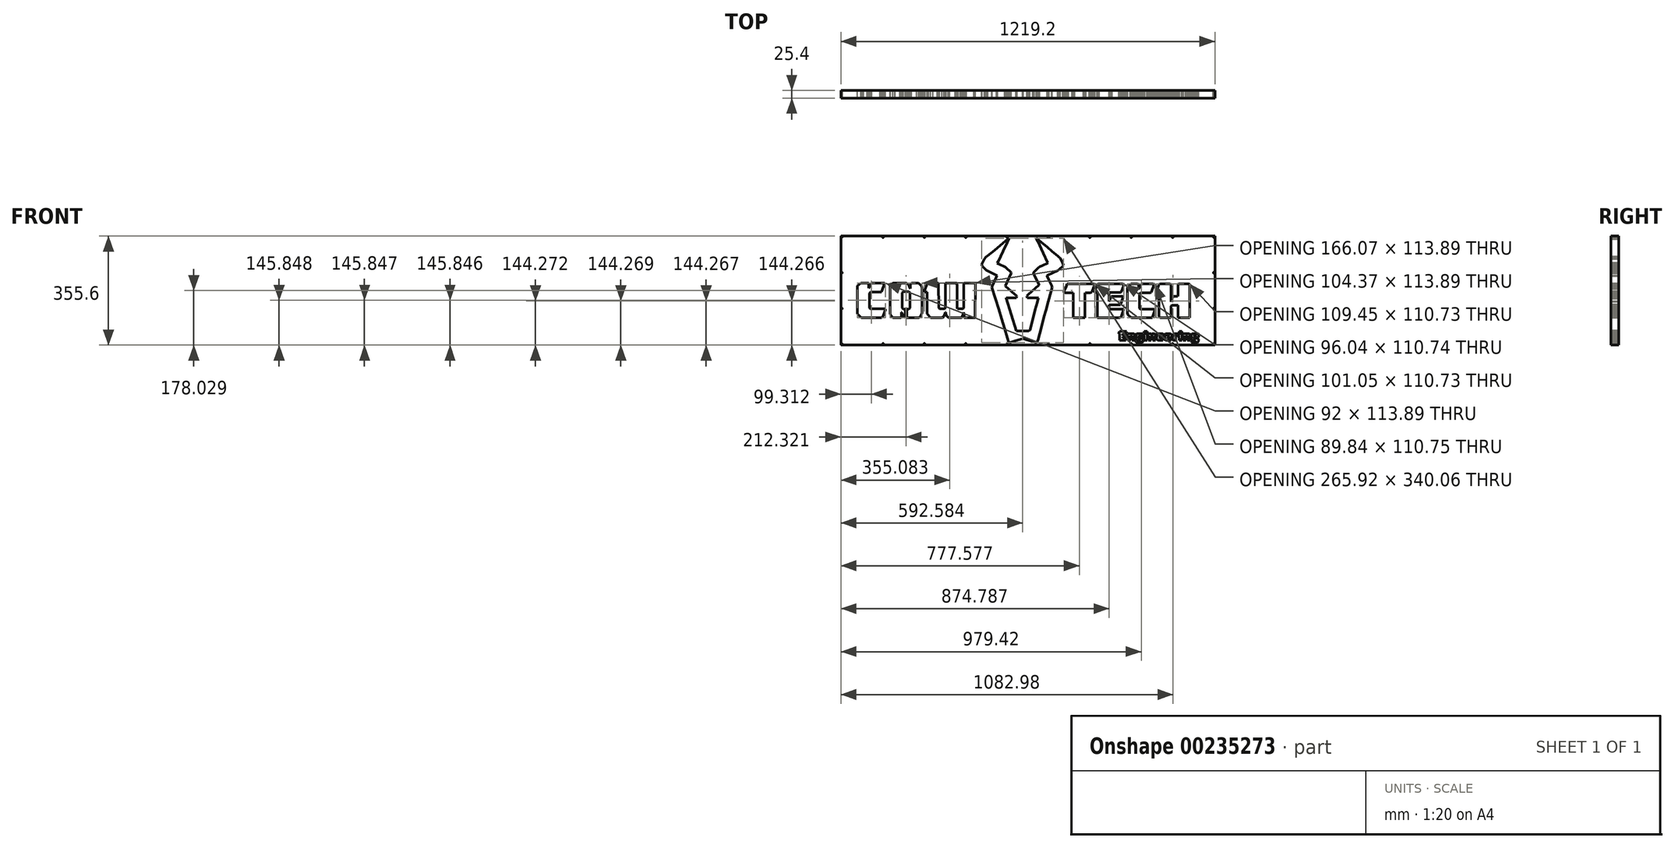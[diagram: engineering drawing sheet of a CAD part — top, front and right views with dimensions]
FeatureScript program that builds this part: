
annotation { "Feature Type Name" : "Feature", "Feature Type Description" : "" }
export const myFeature = defineFeature(function(context is Context, id is Id, definition is map)
    precondition{}
    {
        {
            var Q0;
            Q0=qCreatedBy(makeId("Front.planeOp"),FACE);
            var sketch = newSketch(context, id + "F0", { "sketchPlane" : qUnion([Q0])});
            skLineSegment(sketch, "E0.bottom", {"start": v(609.6, -177.8) * mm, "end": v(-609.6, -177.8) * mm});
            skLineSegment(sketch, "E0.top", {"start": v(609.6, 177.8) * mm, "end": v(-609.6, 177.8) * mm});
            skLineSegment(sketch, "E0.left", {"start": v(609.6, -177.8) * mm, "end": v(609.6, 177.8) * mm});
            skLineSegment(sketch, "E0.right", {"start": v(-609.6, -177.8) * mm, "end": v(-609.6, 177.8) * mm});
            skPoint(sketch, "E0.middle", {"position": v(0, 0) * mm});
            skLineSegment(sketch, "E1.top", {"start": v(-606.8, -175) * mm, "end": v(606.8, -175) * mm});
            skLineSegment(sketch, "E1.left", {"start": v(-606.8, 175) * mm, "end": v(-606.8, -175) * mm});
            skLineSegment(sketch, "E1.right", {"start": v(606.8, 175) * mm, "end": v(606.8, -175) * mm});
            skCircle(sketch, "E2", {"center": v(-606.8, 175) * mm, "radius": 2.29 * mm});
            skCircle(sketch, "E3.1.0.0", {"center": v(-471.96, 175) * mm, "radius": 2.29 * mm});
            skCircle(sketch, "E3.2.0.0", {"center": v(-337.11, 175) * mm, "radius": 2.29 * mm});
            skCircle(sketch, "E3.3.0.0", {"center": v(-202.27, 175) * mm, "radius": 2.29 * mm});
            skCircle(sketch, "E3.4.0.0", {"center": v(-67.42, 175) * mm, "radius": 2.29 * mm});
            skCircle(sketch, "E3.5.0.0", {"center": v(67.42, 175) * mm, "radius": 2.29 * mm});
            skCircle(sketch, "E3.6.0.0", {"center": v(202.27, 175) * mm, "radius": 2.29 * mm});
            skCircle(sketch, "E3.7.0.0", {"center": v(337.11, 175) * mm, "radius": 2.29 * mm});
            skCircle(sketch, "E3.8.0.0", {"center": v(471.96, 175) * mm, "radius": 2.29 * mm});
            skCircle(sketch, "E3.9.0.0", {"center": v(606.8, 175) * mm, "radius": 2.29 * mm});
            skLineSegment(sketch, "E3.direction1", {"start": v(-606.8, 175) * mm, "end": v(-471.96, 175) * mm, "construction": true});
            skLineSegment(sketch, "E4", {"start": v(0, 0) * mm, "end": v(-450.1, 0) * mm, "construction": true});
            skCircle(sketch, "E5.MirrorC", {"center": v(-471.96, -175) * mm, "radius": 2.29 * mm});
            skCircle(sketch, "E6.MirrorC", {"center": v(-606.8, -175) * mm, "radius": 2.29 * mm});
            skCircle(sketch, "E7.MirrorC", {"center": v(-337.11, -175) * mm, "radius": 2.29 * mm});
            skCircle(sketch, "E8.MirrorC", {"center": v(-202.27, -175) * mm, "radius": 2.29 * mm});
            skCircle(sketch, "E9.MirrorC", {"center": v(-67.42, -175) * mm, "radius": 2.29 * mm});
            skCircle(sketch, "E10.MirrorC", {"center": v(67.42, -175) * mm, "radius": 2.29 * mm});
            skCircle(sketch, "E11.MirrorC", {"center": v(202.27, -175) * mm, "radius": 2.29 * mm});
            skCircle(sketch, "E12.MirrorC", {"center": v(337.11, -175) * mm, "radius": 2.29 * mm});
            skCircle(sketch, "E13.MirrorC", {"center": v(471.96, -175) * mm, "radius": 2.29 * mm});
            skCircle(sketch, "E14.MirrorC", {"center": v(606.8, -175) * mm, "radius": 2.29 * mm});
            skCircle(sketch, "E15.1.0.0", {"center": v(-606.8, 58.34) * mm, "radius": 2.29 * mm});
            skCircle(sketch, "E15.2.0.0", {"center": v(-606.8, -58.34) * mm, "radius": 2.29 * mm});
            skLineSegment(sketch, "E15.direction1", {"start": v(-606.8, 175) * mm, "end": v(-606.8, 58.34) * mm, "construction": true});
            skLineSegment(sketch, "E16", {"start": v(0, 0) * mm, "end": v(0, 134.11) * mm, "construction": true});
            skCircle(sketch, "E17.MirrorC", {"center": v(606.8, 58.34) * mm, "radius": 2.29 * mm});
            skCircle(sketch, "E18.MirrorC", {"center": v(606.8, -58.34) * mm, "radius": 2.29 * mm});
            skSolve(sketch);
        }
        {
            var Q0;
            Q0=makeQuery(id+"F0.imprint","IMPRINT",FACE,{"disambiguationData":[TD([[makeQuery(id+"F0.imprint","IMPRINT",EDGE,{"derivedFrom":sQuery(id+"F0.wireOp",EDGE,"E0.bottom")}),-1.0]])]});
            var sketch = newSketch(context, id + "F1", { "sketchPlane" : qUnion([Q0])});
            skLineSegment(sketch, "E19", {"start": v(30.23, -169.78) * mm, "end": v(23.8, -168.03) * mm});
            skLineSegment(sketch, "E20", {"start": v(23.8, -168.03) * mm, "end": v(-7.37, -159.28) * mm});
            skLineSegment(sketch, "E21", {"start": v(-7.37, -159.28) * mm, "end": v(-14.2, -157.3) * mm});
            skLineSegment(sketch, "E22", {"start": v(-14.2, -157.3) * mm, "end": v(-16.57, -157.28) * mm});
            skLineSegment(sketch, "E23", {"start": v(-16.57, -157.28) * mm, "end": v(-40.15, -164.01) * mm});
            skLineSegment(sketch, "E24", {"start": v(-40.15, -164.01) * mm, "end": v(-59.48, -169.5) * mm});
            skLineSegment(sketch, "E25", {"start": v(-59.48, -169.5) * mm, "end": v(-60.97, -169.8) * mm});
            skLineSegment(sketch, "E26", {"start": v(-60.97, -169.8) * mm, "end": v(-62.42, -166.98) * mm});
            skLineSegment(sketch, "E27", {"start": v(-62.42, -166.98) * mm, "end": v(-66.22, -154.79) * mm});
            skLineSegment(sketch, "E28", {"start": v(-66.22, -154.79) * mm, "end": v(-75.53, -124.27) * mm});
            skLineSegment(sketch, "E29", {"start": v(-75.53, -124.27) * mm, "end": v(-85.6, -91.16) * mm});
            skLineSegment(sketch, "E30", {"start": v(-85.6, -91.16) * mm, "end": v(-95.08, -60.42) * mm});
            skLineSegment(sketch, "E31", {"start": v(-95.08, -60.42) * mm, "end": v(-105.76, -25.19) * mm});
            skLineSegment(sketch, "E32", {"start": v(-105.76, -25.19) * mm, "end": v(-116.9, 10.67) * mm});
            skLineSegment(sketch, "E33", {"start": v(-116.9, 10.67) * mm, "end": v(-116.63, 13.72) * mm});
            skLineSegment(sketch, "E34", {"start": v(-116.63, 13.72) * mm, "end": v(-103.29, 42.19) * mm});
            skLineSegment(sketch, "E35", {"start": v(-103.29, 42.19) * mm, "end": v(-100.59, 47.97) * mm});
            skLineSegment(sketch, "E36", {"start": v(-100.59, 47.97) * mm, "end": v(-100.17, 49.2) * mm});
            skLineSegment(sketch, "E37", {"start": v(-100.17, 49.2) * mm, "end": v(-101.67, 50.11) * mm});
            skLineSegment(sketch, "E38", {"start": v(-101.67, 50.11) * mm, "end": v(-120.54, 59.03) * mm});
            skLineSegment(sketch, "E39", {"start": v(-120.54, 59.03) * mm, "end": v(-130.76, 63.84) * mm});
            skLineSegment(sketch, "E40", {"start": v(-130.76, 63.84) * mm, "end": v(-135.19, 66.9) * mm});
            skLineSegment(sketch, "E41", {"start": v(-135.19, 66.9) * mm, "end": v(-148.63, 80.22) * mm});
            skLineSegment(sketch, "E42", {"start": v(-148.63, 80.22) * mm, "end": v(-149.7, 81.57) * mm});
            skLineSegment(sketch, "E43", {"start": v(-149.7, 81.57) * mm, "end": v(-149.98, 85.04) * mm});
            skLineSegment(sketch, "E44", {"start": v(-149.98, 85.04) * mm, "end": v(-147.5, 90.38) * mm});
            skLineSegment(sketch, "E45", {"start": v(-147.5, 90.38) * mm, "end": v(-141.5, 103.31) * mm});
            skLineSegment(sketch, "E46", {"start": v(-141.5, 103.31) * mm, "end": v(-137.04, 109.06) * mm});
            skLineSegment(sketch, "E47", {"start": v(-137.04, 109.06) * mm, "end": v(-115.55, 126.68) * mm});
            skLineSegment(sketch, "E48", {"start": v(-115.55, 126.68) * mm, "end": v(-100.34, 139.14) * mm});
            skLineSegment(sketch, "E49", {"start": v(-100.34, 139.14) * mm, "end": v(-71.43, 162.81) * mm});
            skLineSegment(sketch, "E50", {"start": v(-71.43, 162.81) * mm, "end": v(-63.4, 169.3) * mm});
            skLineSegment(sketch, "E51", {"start": v(-63.4, 169.3) * mm, "end": v(-61.47, 170.18) * mm});
            skLineSegment(sketch, "E52", {"start": v(-61.47, 170.18) * mm, "end": v(-61.97, 168.1) * mm});
            skLineSegment(sketch, "E53", {"start": v(-61.97, 168.1) * mm, "end": v(-66.6, 158.34) * mm});
            skLineSegment(sketch, "E54", {"start": v(-66.6, 158.34) * mm, "end": v(-80.63, 128.83) * mm});
            skLineSegment(sketch, "E55", {"start": v(-80.63, 128.83) * mm, "end": v(-96.44, 95.54) * mm});
            skLineSegment(sketch, "E56", {"start": v(-96.44, 95.54) * mm, "end": v(-99.34, 89.4) * mm});
            skLineSegment(sketch, "E57", {"start": v(-99.34, 89.4) * mm, "end": v(-97.9, 88.08) * mm});
            skLineSegment(sketch, "E58", {"start": v(-97.9, 88.08) * mm, "end": v(-91.68, 85.14) * mm});
            skLineSegment(sketch, "E59", {"start": v(-91.68, 85.14) * mm, "end": v(-75.87, 77.81) * mm});
            skLineSegment(sketch, "E60", {"start": v(-75.87, 77.81) * mm, "end": v(-73.22, 76.53) * mm});
            skLineSegment(sketch, "E61", {"start": v(-73.22, 76.53) * mm, "end": v(-70.04, 74.26) * mm});
            skLineSegment(sketch, "E62", {"start": v(-70.04, 74.26) * mm, "end": v(-55.8, 59.98) * mm});
            skLineSegment(sketch, "E63", {"start": v(-55.8, 59.98) * mm, "end": v(-53.65, 57.54) * mm});
            skLineSegment(sketch, "E64", {"start": v(-53.65, 57.54) * mm, "end": v(-73.23, 15.55) * mm});
            skLineSegment(sketch, "E65", {"start": v(-73.23, 15.55) * mm, "end": v(-71.4, 13.34) * mm});
            skLineSegment(sketch, "E66", {"start": v(-71.4, 13.34) * mm, "end": v(-63.63, 6.53) * mm});
            skLineSegment(sketch, "E67", {"start": v(-63.63, 6.53) * mm, "end": v(-42.1, -12.55) * mm});
            skLineSegment(sketch, "E68", {"start": v(-42.1, -12.55) * mm, "end": v(-37.9, -16.32) * mm});
            skLineSegment(sketch, "E69", {"start": v(-37.9, -16.32) * mm, "end": v(-36.86, -18.7) * mm});
            skLineSegment(sketch, "E70", {"start": v(-36.86, -18.7) * mm, "end": v(-37.04, -23.65) * mm});
            skLineSegment(sketch, "E71", {"start": v(-37.04, -23.65) * mm, "end": v(-39.3, -24.2) * mm});
            skLineSegment(sketch, "E72", {"start": v(-39.3, -24.2) * mm, "end": v(-63.15, -24.17) * mm});
            skLineSegment(sketch, "E73", {"start": v(-63.15, -24.17) * mm, "end": v(-68.56, -24.16) * mm});
            skLineSegment(sketch, "E74", {"start": v(-68.56, -24.16) * mm, "end": v(-70.2, -24.4) * mm});
            skLineSegment(sketch, "E75", {"start": v(-70.2, -24.4) * mm, "end": v(-70.3, -25.24) * mm});
            skLineSegment(sketch, "E76", {"start": v(-70.3, -25.24) * mm, "end": v(-37.92, -131.17) * mm});
            skLineSegment(sketch, "E77", {"start": v(-37.92, -131.17) * mm, "end": v(-35.1, -131.64) * mm});
            skLineSegment(sketch, "E78", {"start": v(-35.1, -131.64) * mm, "end": v(-22.05, -131.65) * mm});
            skLineSegment(sketch, "E79", {"start": v(-22.05, -131.65) * mm, "end": v(2.79, -131.65) * mm});
            skLineSegment(sketch, "E80", {"start": v(2.79, -131.65) * mm, "end": v(6.44, -128.86) * mm});
            skLineSegment(sketch, "E81", {"start": v(6.44, -128.86) * mm, "end": v(16.74, -90.46) * mm});
            skLineSegment(sketch, "E82", {"start": v(16.74, -90.46) * mm, "end": v(23.97, -63.43) * mm});
            skLineSegment(sketch, "E83", {"start": v(23.97, -63.43) * mm, "end": v(30.71, -38.05) * mm});
            skLineSegment(sketch, "E84", {"start": v(30.71, -38.05) * mm, "end": v(34.05, -25.73) * mm});
            skLineSegment(sketch, "E85", {"start": v(34.05, -25.73) * mm, "end": v(34.47, -23.95) * mm});
            skLineSegment(sketch, "E86", {"start": v(34.47, -23.95) * mm, "end": v(25.31, -24.01) * mm});
            skLineSegment(sketch, "E87", {"start": v(25.31, -24.01) * mm, "end": v(16.22, -24.14) * mm});
            skLineSegment(sketch, "E88", {"start": v(16.22, -24.14) * mm, "end": v(7.12, -24.15) * mm});
            skLineSegment(sketch, "E89", {"start": v(7.12, -24.15) * mm, "end": v(-1.94, -24.11) * mm});
            skLineSegment(sketch, "E90", {"start": v(-1.94, -24.11) * mm, "end": v(-2.7, -17.5) * mm});
            skLineSegment(sketch, "E91", {"start": v(-2.7, -17.5) * mm, "end": v(-2.02, -16.25) * mm});
            skLineSegment(sketch, "E92", {"start": v(-2.02, -16.25) * mm, "end": v(0.16, -14.27) * mm});
            skLineSegment(sketch, "E93", {"start": v(0.16, -14.27) * mm, "end": v(25.23, 7.85) * mm});
            skLineSegment(sketch, "E94", {"start": v(25.23, 7.85) * mm, "end": v(34.84, 16.29) * mm});
            skLineSegment(sketch, "E95", {"start": v(34.84, 16.29) * mm, "end": v(36.37, 17.75) * mm});
            skLineSegment(sketch, "E96", {"start": v(36.37, 17.75) * mm, "end": v(35.74, 19.52) * mm});
            skLineSegment(sketch, "E97", {"start": v(35.74, 19.52) * mm, "end": v(21.07, 50.9) * mm});
            skLineSegment(sketch, "E98", {"start": v(21.07, 50.9) * mm, "end": v(18.53, 56.5) * mm});
            skLineSegment(sketch, "E99", {"start": v(18.53, 56.5) * mm, "end": v(18.85, 58.73) * mm});
            skLineSegment(sketch, "E100", {"start": v(18.85, 58.73) * mm, "end": v(20.87, 60.88) * mm});
            skLineSegment(sketch, "E101", {"start": v(20.87, 60.88) * mm, "end": v(34.76, 74.81) * mm});
            skLineSegment(sketch, "E102", {"start": v(34.76, 74.81) * mm, "end": v(38.96, 77.77) * mm});
            skLineSegment(sketch, "E103", {"start": v(38.96, 77.77) * mm, "end": v(48.1, 81.96) * mm});
            skLineSegment(sketch, "E104", {"start": v(48.1, 81.96) * mm, "end": v(63.89, 89.36) * mm});
            skLineSegment(sketch, "E105", {"start": v(63.89, 89.36) * mm, "end": v(65.07, 90.07) * mm});
            skLineSegment(sketch, "E106", {"start": v(65.07, 90.07) * mm, "end": v(64.62, 91.66) * mm});
            skLineSegment(sketch, "E107", {"start": v(64.62, 91.66) * mm, "end": v(50.38, 121.88) * mm});
            skLineSegment(sketch, "E108", {"start": v(50.38, 121.88) * mm, "end": v(31.98, 161) * mm});
            skLineSegment(sketch, "E109", {"start": v(31.98, 161) * mm, "end": v(28.5, 168.33) * mm});
            skLineSegment(sketch, "E110", {"start": v(28.5, 168.33) * mm, "end": v(27.95, 170.26) * mm});
            skLineSegment(sketch, "E111", {"start": v(27.95, 170.26) * mm, "end": v(29.5, 169.48) * mm});
            skLineSegment(sketch, "E112", {"start": v(29.5, 169.48) * mm, "end": v(43.55, 157.93) * mm});
            skLineSegment(sketch, "E113", {"start": v(43.55, 157.93) * mm, "end": v(64.17, 140.8) * mm});
            skLineSegment(sketch, "E114", {"start": v(64.17, 140.8) * mm, "end": v(78.56, 128.9) * mm});
            skLineSegment(sketch, "E115", {"start": v(78.56, 128.9) * mm, "end": v(98.53, 112.54) * mm});
            skLineSegment(sketch, "E116", {"start": v(98.53, 112.54) * mm, "end": v(102.86, 108.9) * mm});
            skLineSegment(sketch, "E117", {"start": v(102.86, 108.9) * mm, "end": v(105.66, 105.22) * mm});
            skLineSegment(sketch, "E118", {"start": v(105.66, 105.22) * mm, "end": v(113.07, 89.43) * mm});
            skLineSegment(sketch, "E119", {"start": v(113.07, 89.43) * mm, "end": v(115.95, 83.17) * mm});
            skLineSegment(sketch, "E120", {"start": v(115.95, 83.17) * mm, "end": v(113.23, 79.66) * mm});
            skLineSegment(sketch, "E121", {"start": v(113.23, 79.66) * mm, "end": v(103.17, 69.55) * mm});
            skLineSegment(sketch, "E122", {"start": v(103.17, 69.55) * mm, "end": v(97.19, 65.33) * mm});
            skLineSegment(sketch, "E123", {"start": v(97.19, 65.33) * mm, "end": v(64.08, 49.76) * mm});
            skLineSegment(sketch, "E124", {"start": v(64.08, 49.76) * mm, "end": v(62.67, 49.02) * mm});
            skLineSegment(sketch, "E125", {"start": v(62.67, 49.02) * mm, "end": v(63.09, 46.83) * mm});
            skLineSegment(sketch, "E126", {"start": v(63.09, 46.83) * mm, "end": v(71.73, 28.37) * mm});
            skLineSegment(sketch, "E127", {"start": v(71.73, 28.37) * mm, "end": v(77.47, 16.14) * mm});
            skLineSegment(sketch, "E128", {"start": v(77.47, 16.14) * mm, "end": v(78.48, 13.9) * mm});
            skLineSegment(sketch, "E129", {"start": v(78.48, 13.9) * mm, "end": v(78.73, 10.1) * mm});
            skLineSegment(sketch, "E130", {"start": v(78.73, 10.1) * mm, "end": v(74.92, -3.87) * mm});
            skLineSegment(sketch, "E131", {"start": v(74.92, -3.87) * mm, "end": v(66.64, -34.94) * mm});
            skLineSegment(sketch, "E132", {"start": v(66.64, -34.94) * mm, "end": v(58.69, -64.32) * mm});
            skLineSegment(sketch, "E133", {"start": v(58.69, -64.32) * mm, "end": v(53.13, -85.2) * mm});
            skLineSegment(sketch, "E134", {"start": v(53.13, -85.2) * mm, "end": v(43.46, -121.22) * mm});
            skLineSegment(sketch, "E135", {"start": v(43.46, -121.22) * mm, "end": v(33.08, -159.87) * mm});
            skLineSegment(sketch, "E136", {"start": v(33.08, -159.87) * mm, "end": v(31.36, -166.52) * mm});
            skLineSegment(sketch, "E137", {"start": v(31.36, -166.52) * mm, "end": v(30.23, -169.78) * mm});
            skLineSegment(sketch, "E138", {"start": v(-208.3, 24.16) * mm, "end": v(-204.68, 24.98) * mm});
            skLineSegment(sketch, "E139", {"start": v(-204.68, 24.98) * mm, "end": v(-175.42, 24.98) * mm});
            skLineSegment(sketch, "E140", {"start": v(-175.42, 24.98) * mm, "end": v(-171.73, 24.14) * mm});
            skLineSegment(sketch, "E141", {"start": v(-171.73, 24.14) * mm, "end": v(-171.48, 22.8) * mm});
            skLineSegment(sketch, "E142", {"start": v(-171.48, 22.8) * mm, "end": v(-171.52, -87.12) * mm});
            skLineSegment(sketch, "E143", {"start": v(-171.52, -87.12) * mm, "end": v(-171.9, -88.4) * mm});
            skLineSegment(sketch, "E144", {"start": v(-171.9, -88.4) * mm, "end": v(-174.72, -88.86) * mm});
            skLineSegment(sketch, "E145", {"start": v(-174.72, -88.86) * mm, "end": v(-204.36, -88.87) * mm});
            skLineSegment(sketch, "E146", {"start": v(-204.36, -88.87) * mm, "end": v(-207.65, -87.94) * mm});
            skLineSegment(sketch, "E147", {"start": v(-207.65, -87.94) * mm, "end": v(-207.98, -79.5) * mm});
            skLineSegment(sketch, "E148", {"start": v(-207.98, -79.5) * mm, "end": v(-208.5, -70.9) * mm});
            skLineSegment(sketch, "E149", {"start": v(-208.5, -70.9) * mm, "end": v(-209.25, -72.45) * mm});
            skLineSegment(sketch, "E150", {"start": v(-209.25, -72.45) * mm, "end": v(-214.5, -84.87) * mm});
            skLineSegment(sketch, "E151", {"start": v(-214.5, -84.87) * mm, "end": v(-215.58, -87.26) * mm});
            skLineSegment(sketch, "E152", {"start": v(-215.58, -87.26) * mm, "end": v(-217.59, -88.72) * mm});
            skLineSegment(sketch, "E153", {"start": v(-217.59, -88.72) * mm, "end": v(-220.58, -88.9) * mm});
            skLineSegment(sketch, "E154", {"start": v(-220.58, -88.9) * mm, "end": v(-254.34, -88.88) * mm});
            skLineSegment(sketch, "E155", {"start": v(-254.34, -88.88) * mm, "end": v(-258.82, -88.5) * mm});
            skLineSegment(sketch, "E156", {"start": v(-258.82, -88.5) * mm, "end": v(-266.47, -81.36) * mm});
            skLineSegment(sketch, "E157", {"start": v(-266.47, -81.36) * mm, "end": v(-267.26, -74.3) * mm});
            skLineSegment(sketch, "E158", {"start": v(-267.26, -74.3) * mm, "end": v(-267.28, -70.23) * mm});
            skLineSegment(sketch, "E159", {"start": v(-267.28, -70.23) * mm, "end": v(-268.39, -71.11) * mm});
            skLineSegment(sketch, "E160", {"start": v(-268.39, -71.11) * mm, "end": v(-274.05, -84.59) * mm});
            skLineSegment(sketch, "E161", {"start": v(-274.05, -84.59) * mm, "end": v(-280.66, -88.9) * mm});
            skLineSegment(sketch, "E162", {"start": v(-280.66, -88.9) * mm, "end": v(-291.53, -88.9) * mm});
            skLineSegment(sketch, "E163", {"start": v(-291.53, -88.9) * mm, "end": v(-309.54, -88.88) * mm});
            skLineSegment(sketch, "E164", {"start": v(-309.54, -88.88) * mm, "end": v(-317.01, -88.4) * mm});
            skLineSegment(sketch, "E165", {"start": v(-317.01, -88.4) * mm, "end": v(-328.06, -75.8) * mm});
            skLineSegment(sketch, "E166", {"start": v(-328.06, -75.8) * mm, "end": v(-328.23, -68.3) * mm});
            skLineSegment(sketch, "E167", {"start": v(-328.23, -68.3) * mm, "end": v(-328.25, -9.4) * mm});
            skLineSegment(sketch, "E168", {"start": v(-328.25, -9.4) * mm, "end": v(-328.75, -4.8) * mm});
            skLineSegment(sketch, "E169", {"start": v(-328.75, -4.8) * mm, "end": v(-337.55, -4.2) * mm});
            skLineSegment(sketch, "E170", {"start": v(-337.55, -4.2) * mm, "end": v(-337.47, -1.32) * mm});
            skLineSegment(sketch, "E171", {"start": v(-337.47, -1.32) * mm, "end": v(-330.82, 15.79) * mm});
            skLineSegment(sketch, "E172", {"start": v(-330.82, 15.79) * mm, "end": v(-328.78, 21.02) * mm});
            skLineSegment(sketch, "E173", {"start": v(-328.78, 21.02) * mm, "end": v(-327.17, 24.6) * mm});
            skLineSegment(sketch, "E174", {"start": v(-327.17, 24.6) * mm, "end": v(-323.07, 24.97) * mm});
            skLineSegment(sketch, "E175", {"start": v(-323.07, 24.97) * mm, "end": v(-295.31, 24.98) * mm});
            skLineSegment(sketch, "E176", {"start": v(-295.31, 24.98) * mm, "end": v(-291.27, 24.25) * mm});
            skLineSegment(sketch, "E177", {"start": v(-291.27, 24.25) * mm, "end": v(-290.88, 19.48) * mm});
            skLineSegment(sketch, "E178", {"start": v(-290.88, 19.48) * mm, "end": v(-290.87, -52.93) * mm});
            skLineSegment(sketch, "E179", {"start": v(-290.87, -52.93) * mm, "end": v(-290.82, -56.3) * mm});
            skLineSegment(sketch, "E180", {"start": v(-290.82, -56.3) * mm, "end": v(-287.45, -59.5) * mm});
            skLineSegment(sketch, "E181", {"start": v(-287.45, -59.5) * mm, "end": v(-271.7, -59.5) * mm});
            skLineSegment(sketch, "E182", {"start": v(-271.7, -59.5) * mm, "end": v(-268.8, -56.5) * mm});
            skLineSegment(sketch, "E183", {"start": v(-268.8, -56.5) * mm, "end": v(-268.78, -53.13) * mm});
            skLineSegment(sketch, "E184", {"start": v(-268.78, -53.13) * mm, "end": v(-268.77, 19.27) * mm});
            skLineSegment(sketch, "E185", {"start": v(-268.77, 19.27) * mm, "end": v(-268.61, 24.22) * mm});
            skLineSegment(sketch, "E186", {"start": v(-268.61, 24.22) * mm, "end": v(-265.96, 24.9) * mm});
            skLineSegment(sketch, "E187", {"start": v(-265.96, 24.9) * mm, "end": v(-260.34, 25) * mm});
            skLineSegment(sketch, "E188", {"start": v(-260.34, 25) * mm, "end": v(-236.33, 24.98) * mm});
            skLineSegment(sketch, "E189", {"start": v(-236.33, 24.98) * mm, "end": v(-231.75, 24.7) * mm});
            skLineSegment(sketch, "E190", {"start": v(-231.75, 24.7) * mm, "end": v(-231.11, 22.07) * mm});
            skLineSegment(sketch, "E191", {"start": v(-231.11, 22.07) * mm, "end": v(-231.06, 18.32) * mm});
            skLineSegment(sketch, "E192", {"start": v(-231.06, 18.32) * mm, "end": v(-231.05, -52.96) * mm});
            skLineSegment(sketch, "E193", {"start": v(-231.05, -52.96) * mm, "end": v(-230.93, -57.08) * mm});
            skLineSegment(sketch, "E194", {"start": v(-230.93, -57.08) * mm, "end": v(-228.8, -59.35) * mm});
            skLineSegment(sketch, "E195", {"start": v(-228.8, -59.35) * mm, "end": v(-226.57, -59.53) * mm});
            skLineSegment(sketch, "E196", {"start": v(-226.57, -59.53) * mm, "end": v(-212.7, -59.53) * mm});
            skLineSegment(sketch, "E197", {"start": v(-212.7, -59.53) * mm, "end": v(-211.2, -59.46) * mm});
            skLineSegment(sketch, "E198", {"start": v(-211.2, -59.46) * mm, "end": v(-208.8, -57.13) * mm});
            skLineSegment(sketch, "E199", {"start": v(-208.8, -57.13) * mm, "end": v(-208.74, -53.38) * mm});
            skLineSegment(sketch, "E200", {"start": v(-208.74, -53.38) * mm, "end": v(-208.73, 19.4) * mm});
            skLineSegment(sketch, "E201", {"start": v(-208.73, 19.4) * mm, "end": v(-208.3, 24.16) * mm});
            skLineSegment(sketch, "E202", {"start": v(-411.92, -70.4) * mm, "end": v(-411.93, -83.89) * mm});
            skLineSegment(sketch, "E203", {"start": v(-411.93, -83.89) * mm, "end": v(-412.13, -87.25) * mm});
            skLineSegment(sketch, "E204", {"start": v(-412.13, -87.25) * mm, "end": v(-413.62, -88.69) * mm});
            skLineSegment(sketch, "E205", {"start": v(-413.62, -88.69) * mm, "end": v(-416.6, -88.89) * mm});
            skLineSegment(sketch, "E206", {"start": v(-416.6, -88.89) * mm, "end": v(-433.86, -88.87) * mm});
            skLineSegment(sketch, "E207", {"start": v(-433.86, -88.87) * mm, "end": v(-440.16, -88.15) * mm});
            skLineSegment(sketch, "E208", {"start": v(-440.16, -88.15) * mm, "end": v(-448.86, -77.51) * mm});
            skLineSegment(sketch, "E209", {"start": v(-448.86, -77.51) * mm, "end": v(-449.46, -69.3) * mm});
            skLineSegment(sketch, "E210", {"start": v(-449.46, -69.3) * mm, "end": v(-449.46, 6.06) * mm});
            skLineSegment(sketch, "E211", {"start": v(-449.46, 6.06) * mm, "end": v(-448.87, 14.65) * mm});
            skLineSegment(sketch, "E212", {"start": v(-448.87, 14.65) * mm, "end": v(-448.17, 17.56) * mm});
            skLineSegment(sketch, "E213", {"start": v(-448.17, 17.56) * mm, "end": v(-439.78, 24.54) * mm});
            skLineSegment(sketch, "E214", {"start": v(-439.78, 24.54) * mm, "end": v(-433.05, 24.98) * mm});
            skLineSegment(sketch, "E215", {"start": v(-433.05, 24.98) * mm, "end": v(-396.3, 25) * mm});
            skLineSegment(sketch, "E216", {"start": v(-396.3, 25) * mm, "end": v(-389.27, 20.19) * mm});
            skLineSegment(sketch, "E217", {"start": v(-389.27, 20.19) * mm, "end": v(-383.95, 7.4) * mm});
            skLineSegment(sketch, "E218", {"start": v(-383.95, 7.4) * mm, "end": v(-383.27, 6.14) * mm});
            skLineSegment(sketch, "E219", {"start": v(-383.27, 6.14) * mm, "end": v(-382.72, 8.28) * mm});
            skLineSegment(sketch, "E220", {"start": v(-382.72, 8.28) * mm, "end": v(-382.68, 21.02) * mm});
            skLineSegment(sketch, "E221", {"start": v(-382.68, 21.02) * mm, "end": v(-378.85, 24.96) * mm});
            skLineSegment(sketch, "E222", {"start": v(-378.85, 24.96) * mm, "end": v(-356.75, 24.61) * mm});
            skLineSegment(sketch, "E223", {"start": v(-356.75, 24.61) * mm, "end": v(-345.78, 14.65) * mm});
            skLineSegment(sketch, "E224", {"start": v(-345.78, 14.65) * mm, "end": v(-345.16, 7.95) * mm});
            skLineSegment(sketch, "E225", {"start": v(-345.16, 7.95) * mm, "end": v(-345.1, -73.42) * mm});
            skLineSegment(sketch, "E226", {"start": v(-345.1, -73.42) * mm, "end": v(-351.63, -86.55) * mm});
            skLineSegment(sketch, "E227", {"start": v(-351.63, -86.55) * mm, "end": v(-356.82, -88.51) * mm});
            skLineSegment(sketch, "E228", {"start": v(-356.82, -88.51) * mm, "end": v(-362.8, -88.88) * mm});
            skLineSegment(sketch, "E229", {"start": v(-362.8, -88.88) * mm, "end": v(-394.18, -88.9) * mm});
            skLineSegment(sketch, "E230", {"start": v(-399.27, -88.57) * mm, "end": v(-405.76, -84.1) * mm});
            skLineSegment(sketch, "E231", {"start": v(-405.76, -84.1) * mm, "end": v(-410.61, -71.92) * mm});
            skLineSegment(sketch, "E232", {"start": v(-410.61, -71.92) * mm, "end": v(-411.34, -70.27) * mm});
            skLineSegment(sketch, "E233", {"start": v(-411.34, -70.27) * mm, "end": v(-411.92, -70.4) * mm});
            skLineSegment(sketch, "E234", {"start": v(-384.52, -32.17) * mm, "end": v(-384.53, -10.04) * mm});
            skLineSegment(sketch, "E235", {"start": v(-384.53, -10.04) * mm, "end": v(-384.65, -7.05) * mm});
            skLineSegment(sketch, "E236", {"start": v(-384.65, -7.05) * mm, "end": v(-388.47, -3.7) * mm});
            skLineSegment(sketch, "E237", {"start": v(-388.47, -3.7) * mm, "end": v(-392.22, -3.68) * mm});
            skLineSegment(sketch, "E238", {"start": v(-392.22, -3.68) * mm, "end": v(-394.77, -3.69) * mm});
            skLineSegment(sketch, "E239", {"start": v(-405.36, -3.71) * mm, "end": v(-409.54, -7.55) * mm});
            skLineSegment(sketch, "E240", {"start": v(-409.54, -7.55) * mm, "end": v(-409.67, -11.3) * mm});
            skLineSegment(sketch, "E241", {"start": v(-409.67, -11.3) * mm, "end": v(-409.67, -52.94) * mm});
            skLineSegment(sketch, "E242", {"start": v(-409.67, -52.94) * mm, "end": v(-409.58, -56.31) * mm});
            skLineSegment(sketch, "E243", {"start": v(-409.58, -56.31) * mm, "end": v(-405.51, -60.19) * mm});
            skLineSegment(sketch, "E244", {"start": v(-405.51, -60.19) * mm, "end": v(-399.27, -60.2) * mm});
            skLineSegment(sketch, "E245", {"start": v(-394.27, -60.21) * mm, "end": v(-388.63, -60.2) * mm});
            skLineSegment(sketch, "E246", {"start": v(-388.63, -60.2) * mm, "end": v(-384.6, -56.56) * mm});
            skLineSegment(sketch, "E247", {"start": v(-384.6, -56.56) * mm, "end": v(-384.53, -53.56) * mm});
            skLineSegment(sketch, "E248", {"start": v(-384.53, -53.56) * mm, "end": v(-384.52, -32.17) * mm});
            skLineSegment(sketch, "E249", {"start": v(527.84, -88.1) * mm, "end": v(524.24, -88.89) * mm});
            skLineSegment(sketch, "E250", {"start": v(524.24, -88.89) * mm, "end": v(493.6, -88.9) * mm});
            skLineSegment(sketch, "E251", {"start": v(493.6, -88.9) * mm, "end": v(489.84, -88) * mm});
            skLineSegment(sketch, "E252", {"start": v(489.84, -88) * mm, "end": v(489.72, -84.2) * mm});
            skLineSegment(sketch, "E253", {"start": v(489.72, -84.2) * mm, "end": v(489.7, -52.1) * mm});
            skLineSegment(sketch, "E254", {"start": v(489.7, -52.1) * mm, "end": v(489.61, -48.02) * mm});
            skLineSegment(sketch, "E255", {"start": v(489.61, -48.02) * mm, "end": v(487.44, -47.38) * mm});
            skLineSegment(sketch, "E256", {"start": v(487.44, -47.38) * mm, "end": v(468.84, -47.35) * mm});
            skLineSegment(sketch, "E257", {"start": v(468.84, -47.35) * mm, "end": v(466.23, -49.99) * mm});
            skLineSegment(sketch, "E258", {"start": v(466.23, -49.99) * mm, "end": v(466.21, -52.54) * mm});
            skLineSegment(sketch, "E259", {"start": v(466.21, -52.54) * mm, "end": v(466.2, -84.28) * mm});
            skLineSegment(sketch, "E260", {"start": v(466.2, -84.28) * mm, "end": v(465.81, -88.2) * mm});
            skLineSegment(sketch, "E261", {"start": v(465.81, -88.2) * mm, "end": v(462.27, -88.89) * mm});
            skLineSegment(sketch, "E262", {"start": v(462.27, -88.89) * mm, "end": v(432, -88.9) * mm});
            skLineSegment(sketch, "E263", {"start": v(432, -88.9) * mm, "end": v(431.26, -88.88) * mm});
            skLineSegment(sketch, "E264", {"start": v(431.26, -88.88) * mm, "end": v(427.92, -85.37) * mm});
            skLineSegment(sketch, "E265", {"start": v(427.92, -85.37) * mm, "end": v(427.91, -82.09) * mm});
            skLineSegment(sketch, "E266", {"start": v(427.91, -82.09) * mm, "end": v(427.9, -12.05) * mm});
            skLineSegment(sketch, "E267", {"start": v(427.9, -12.05) * mm, "end": v(427.49, -7.25) * mm});
            skLineSegment(sketch, "E268", {"start": v(427.49, -7.25) * mm, "end": v(418.65, -6.42) * mm});
            skLineSegment(sketch, "E269", {"start": v(418.65, -6.42) * mm, "end": v(419.32, -2.47) * mm});
            skLineSegment(sketch, "E270", {"start": v(419.32, -2.47) * mm, "end": v(426.55, 16.22) * mm});
            skLineSegment(sketch, "E271", {"start": v(426.55, 16.22) * mm, "end": v(428.56, 21.05) * mm});
            skLineSegment(sketch, "E272", {"start": v(428.56, 21.05) * mm, "end": v(432.7, 21.83) * mm});
            skLineSegment(sketch, "E273", {"start": v(432.7, 21.83) * mm, "end": v(461.88, 21.83) * mm});
            skLineSegment(sketch, "E274", {"start": v(461.88, 21.83) * mm, "end": v(465.9, 21.1) * mm});
            skLineSegment(sketch, "E275", {"start": v(465.9, 21.1) * mm, "end": v(466.2, 12.87) * mm});
            skLineSegment(sketch, "E276", {"start": v(466.2, 12.87) * mm, "end": v(466.21, 4.84) * mm});
            skLineSegment(sketch, "E277", {"start": v(466.21, 4.84) * mm, "end": v(466.21, -3.55) * mm});
            skLineSegment(sketch, "E278", {"start": v(466.21, -3.55) * mm, "end": v(466.21, -11.57) * mm});
            skLineSegment(sketch, "E279", {"start": v(466.21, -11.57) * mm, "end": v(466.21, -19.96) * mm});
            skLineSegment(sketch, "E280", {"start": v(466.21, -19.96) * mm, "end": v(466.21, -27.99) * mm});
            skLineSegment(sketch, "E281", {"start": v(466.21, -27.99) * mm, "end": v(466.21, -36.27) * mm});
            skLineSegment(sketch, "E282", {"start": v(466.21, -36.27) * mm, "end": v(466.66, -36.39) * mm});
            skLineSegment(sketch, "E283", {"start": v(466.66, -36.39) * mm, "end": v(467.85, -33.52) * mm});
            skLineSegment(sketch, "E284", {"start": v(467.85, -33.52) * mm, "end": v(471.9, -22.6) * mm});
            skLineSegment(sketch, "E285", {"start": v(471.9, -22.6) * mm, "end": v(472.54, -20.89) * mm});
            skLineSegment(sketch, "E286", {"start": v(472.54, -20.89) * mm, "end": v(475.57, -18.77) * mm});
            skLineSegment(sketch, "E287", {"start": v(475.57, -18.77) * mm, "end": v(485.05, -18.76) * mm});
            skLineSegment(sketch, "E288", {"start": v(485.05, -18.76) * mm, "end": v(488.83, -18.67) * mm});
            skLineSegment(sketch, "E289", {"start": v(488.83, -18.67) * mm, "end": v(489.7, -15) * mm});
            skLineSegment(sketch, "E290", {"start": v(489.7, -15) * mm, "end": v(489.71, 8.7) * mm});
            skLineSegment(sketch, "E291", {"start": v(489.71, 8.7) * mm, "end": v(489.72, 17.82) * mm});
            skLineSegment(sketch, "E292", {"start": v(489.72, 17.82) * mm, "end": v(489.9, 20.88) * mm});
            skLineSegment(sketch, "E293", {"start": v(489.9, 20.88) * mm, "end": v(493.56, 21.82) * mm});
            skLineSegment(sketch, "E294", {"start": v(493.56, 21.82) * mm, "end": v(524.2, 21.82) * mm});
            skLineSegment(sketch, "E295", {"start": v(524.2, 21.82) * mm, "end": v(527.81, 21.08) * mm});
            skLineSegment(sketch, "E296", {"start": v(527.81, 21.08) * mm, "end": v(528.1, 19.73) * mm});
            skLineSegment(sketch, "E297", {"start": v(528.1, 19.73) * mm, "end": v(528.1, -86.79) * mm});
            skLineSegment(sketch, "E298", {"start": v(528.1, -86.79) * mm, "end": v(527.84, -88.1) * mm});
            skLineSegment(sketch, "E299", {"start": v(265.27, -6.04) * mm, "end": v(264.78, -35.6) * mm});
            skLineSegment(sketch, "E300", {"start": v(264.78, -35.6) * mm, "end": v(265.74, -34.22) * mm});
            skLineSegment(sketch, "E301", {"start": v(265.74, -34.22) * mm, "end": v(269.89, -22.94) * mm});
            skLineSegment(sketch, "E302", {"start": v(269.89, -22.94) * mm, "end": v(271.16, -19.84) * mm});
            skLineSegment(sketch, "E303", {"start": v(271.16, -19.84) * mm, "end": v(274.95, -19.04) * mm});
            skLineSegment(sketch, "E304", {"start": v(274.95, -19.04) * mm, "end": v(307.42, -19.04) * mm});
            skLineSegment(sketch, "E305", {"start": v(307.42, -19.04) * mm, "end": v(310.85, -19.4) * mm});
            skLineSegment(sketch, "E306", {"start": v(310.85, -19.4) * mm, "end": v(310.57, -21.72) * mm});
            skLineSegment(sketch, "E307", {"start": v(310.57, -21.72) * mm, "end": v(302.31, -44.7) * mm});
            skLineSegment(sketch, "E308", {"start": v(302.31, -44.7) * mm, "end": v(301.2, -46.75) * mm});
            skLineSegment(sketch, "E309", {"start": v(301.2, -46.75) * mm, "end": v(297.23, -46.9) * mm});
            skLineSegment(sketch, "E310", {"start": v(297.23, -46.9) * mm, "end": v(269.14, -46.91) * mm});
            skLineSegment(sketch, "E311", {"start": v(269.14, -46.91) * mm, "end": v(265.26, -47.2) * mm});
            skLineSegment(sketch, "E312", {"start": v(265.26, -47.2) * mm, "end": v(265.2, -60) * mm});
            skLineSegment(sketch, "E313", {"start": v(265.2, -60) * mm, "end": v(269.4, -60.35) * mm});
            skLineSegment(sketch, "E314", {"start": v(269.4, -60.35) * mm, "end": v(308.08, -60.37) * mm});
            skLineSegment(sketch, "E315", {"start": v(308.08, -60.37) * mm, "end": v(312.52, -60.97) * mm});
            skLineSegment(sketch, "E316", {"start": v(312.52, -60.97) * mm, "end": v(312.26, -63.04) * mm});
            skLineSegment(sketch, "E317", {"start": v(312.26, -63.04) * mm, "end": v(304.33, -86.12) * mm});
            skLineSegment(sketch, "E318", {"start": v(304.33, -86.12) * mm, "end": v(300.68, -88.89) * mm});
            skLineSegment(sketch, "E319", {"start": v(300.68, -88.89) * mm, "end": v(298.12, -88.9) * mm});
            skLineSegment(sketch, "E320", {"start": v(298.12, -88.9) * mm, "end": v(231.73, -88.9) * mm});
            skLineSegment(sketch, "E321", {"start": v(231.73, -88.9) * mm, "end": v(226.74, -88.36) * mm});
            skLineSegment(sketch, "E322", {"start": v(226.74, -88.36) * mm, "end": v(226.2, -84.77) * mm});
            skLineSegment(sketch, "E323", {"start": v(226.2, -84.77) * mm, "end": v(226.2, -62.52) * mm});
            skLineSegment(sketch, "E324", {"start": v(226.2, -62.52) * mm, "end": v(226.18, -11.44) * mm});
            skLineSegment(sketch, "E325", {"start": v(226.18, -11.44) * mm, "end": v(225.61, -7.1) * mm});
            skLineSegment(sketch, "E326", {"start": v(225.61, -7.1) * mm, "end": v(217.17, -6.43) * mm});
            skLineSegment(sketch, "E327", {"start": v(217.17, -6.43) * mm, "end": v(217.2, -4.4) * mm});
            skLineSegment(sketch, "E328", {"start": v(217.2, -4.4) * mm, "end": v(220.03, 3.1) * mm});
            skLineSegment(sketch, "E329", {"start": v(220.03, 3.1) * mm, "end": v(225.6, 17.36) * mm});
            skLineSegment(sketch, "E330", {"start": v(225.6, 17.36) * mm, "end": v(227.22, 21.25) * mm});
            skLineSegment(sketch, "E331", {"start": v(227.22, 21.25) * mm, "end": v(229.97, 21.79) * mm});
            skLineSegment(sketch, "E332", {"start": v(229.97, 21.79) * mm, "end": v(232.52, 21.84) * mm});
            skLineSegment(sketch, "E333", {"start": v(232.52, 21.84) * mm, "end": v(308.04, 21.83) * mm});
            skLineSegment(sketch, "E334", {"start": v(308.04, 21.83) * mm, "end": v(313.2, 21.05) * mm});
            skLineSegment(sketch, "E335", {"start": v(313.2, 21.05) * mm, "end": v(312.63, 18.3) * mm});
            skLineSegment(sketch, "E336", {"start": v(312.63, 18.3) * mm, "end": v(305.44, -2.72) * mm});
            skLineSegment(sketch, "E337", {"start": v(305.44, -2.72) * mm, "end": v(304.78, -4.42) * mm});
            skLineSegment(sketch, "E338", {"start": v(304.78, -4.42) * mm, "end": v(302.6, -6) * mm});
            skLineSegment(sketch, "E339", {"start": v(302.6, -6) * mm, "end": v(299.67, -6.04) * mm});
            skLineSegment(sketch, "E340", {"start": v(299.67, -6.04) * mm, "end": v(269.4, -6.04) * mm});
            skLineSegment(sketch, "E341", {"start": v(269.4, -6.04) * mm, "end": v(265.27, -6.04) * mm});
            skLineSegment(sketch, "E342", {"start": v(414.74, -61.5) * mm, "end": v(405.44, -88.3) * mm});
            skLineSegment(sketch, "E343", {"start": v(405.44, -88.3) * mm, "end": v(402.56, -88.85) * mm});
            skLineSegment(sketch, "E344", {"start": v(402.56, -88.85) * mm, "end": v(399.28, -88.9) * mm});
            skLineSegment(sketch, "E345", {"start": v(399.28, -88.9) * mm, "end": v(343.5, -88.89) * mm});
            skLineSegment(sketch, "E346", {"start": v(343.5, -88.89) * mm, "end": v(336.95, -88.5) * mm});
            skLineSegment(sketch, "E347", {"start": v(336.95, -88.5) * mm, "end": v(325.71, -78.69) * mm});
            skLineSegment(sketch, "E348", {"start": v(325.71, -78.69) * mm, "end": v(324.9, -71.83) * mm});
            skLineSegment(sketch, "E349", {"start": v(324.9, -71.83) * mm, "end": v(324.9, 5.47) * mm});
            skLineSegment(sketch, "E350", {"start": v(324.9, 5.47) * mm, "end": v(325.55, 11.61) * mm});
            skLineSegment(sketch, "E351", {"start": v(325.55, 11.61) * mm, "end": v(336.08, 21.4) * mm});
            skLineSegment(sketch, "E352", {"start": v(336.08, 21.4) * mm, "end": v(344.07, 21.82) * mm});
            skLineSegment(sketch, "E353", {"start": v(344.07, 21.82) * mm, "end": v(356.83, 21.83) * mm});
            skLineSegment(sketch, "E354", {"start": v(356.83, 21.83) * mm, "end": v(360.8, 21.13) * mm});
            skLineSegment(sketch, "E355", {"start": v(360.8, 21.13) * mm, "end": v(361.12, 13.2) * mm});
            skLineSegment(sketch, "E356", {"start": v(361.12, 13.2) * mm, "end": v(361.14, 5.28) * mm});
            skLineSegment(sketch, "E357", {"start": v(361.14, 5.28) * mm, "end": v(362.17, 6.25) * mm});
            skLineSegment(sketch, "E358", {"start": v(362.17, 6.25) * mm, "end": v(367.49, 19.02) * mm});
            skLineSegment(sketch, "E359", {"start": v(367.49, 19.02) * mm, "end": v(371.57, 21.84) * mm});
            skLineSegment(sketch, "E360", {"start": v(371.57, 21.84) * mm, "end": v(378.5, 21.84) * mm});
            skLineSegment(sketch, "E361", {"start": v(378.5, 21.84) * mm, "end": v(407.3, 21.83) * mm});
            skLineSegment(sketch, "E362", {"start": v(407.3, 21.83) * mm, "end": v(411.83, 21.17) * mm});
            skLineSegment(sketch, "E363", {"start": v(411.83, 21.17) * mm, "end": v(402.02, -6.32) * mm});
            skLineSegment(sketch, "E364", {"start": v(402.02, -6.32) * mm, "end": v(398.15, -6.78) * mm});
            skLineSegment(sketch, "E365", {"start": v(398.15, -6.78) * mm, "end": v(369.71, -6.8) * mm});
            skLineSegment(sketch, "E366", {"start": v(369.71, -6.8) * mm, "end": v(367.16, -6.83) * mm});
            skLineSegment(sketch, "E367", {"start": v(367.16, -6.83) * mm, "end": v(363.6, -9.85) * mm});
            skLineSegment(sketch, "E368", {"start": v(363.6, -9.85) * mm, "end": v(363.34, -12.75) * mm});
            skLineSegment(sketch, "E369", {"start": v(363.34, -12.75) * mm, "end": v(363.35, -54.68) * mm});
            skLineSegment(sketch, "E370", {"start": v(363.35, -54.68) * mm, "end": v(363.91, -58.62) * mm});
            skLineSegment(sketch, "E371", {"start": v(363.91, -58.62) * mm, "end": v(365.97, -60.4) * mm});
            skLineSegment(sketch, "E372", {"start": v(365.97, -60.4) * mm, "end": v(369.97, -60.6) * mm});
            skLineSegment(sketch, "E373", {"start": v(369.97, -60.6) * mm, "end": v(409.72, -60.63) * mm});
            skLineSegment(sketch, "E374", {"start": v(409.72, -60.63) * mm, "end": v(414.74, -61.5) * mm});
            skLineSegment(sketch, "E375", {"start": v(-519.26, 24.59) * mm, "end": v(-518.86, 7.76) * mm});
            skLineSegment(sketch, "E376", {"start": v(-518.86, 7.76) * mm, "end": v(-517.88, 9.6) * mm});
            skLineSegment(sketch, "E377", {"start": v(-517.88, 9.6) * mm, "end": v(-512.71, 22.06) * mm});
            skLineSegment(sketch, "E378", {"start": v(-512.71, 22.06) * mm, "end": v(-508.53, 24.98) * mm});
            skLineSegment(sketch, "E379", {"start": v(-508.53, 24.98) * mm, "end": v(-506.65, 25) * mm});
            skLineSegment(sketch, "E380", {"start": v(-506.65, 25) * mm, "end": v(-471.78, 24.98) * mm});
            skLineSegment(sketch, "E381", {"start": v(-471.78, 24.98) * mm, "end": v(-466.98, 24.22) * mm});
            skLineSegment(sketch, "E382", {"start": v(-466.98, 24.22) * mm, "end": v(-467.2, 22.7) * mm});
            skLineSegment(sketch, "E383", {"start": v(-467.2, 22.7) * mm, "end": v(-476.55, -2.97) * mm});
            skLineSegment(sketch, "E384", {"start": v(-476.55, -2.97) * mm, "end": v(-477.5, -4.36) * mm});
            skLineSegment(sketch, "E385", {"start": v(-477.5, -4.36) * mm, "end": v(-481.52, -4.46) * mm});
            skLineSegment(sketch, "E386", {"start": v(-481.52, -4.46) * mm, "end": v(-510.4, -4.46) * mm});
            skLineSegment(sketch, "E387", {"start": v(-510.4, -4.46) * mm, "end": v(-513.02, -4.5) * mm});
            skLineSegment(sketch, "E388", {"start": v(-513.02, -4.5) * mm, "end": v(-516.74, -8.37) * mm});
            skLineSegment(sketch, "E389", {"start": v(-516.74, -8.37) * mm, "end": v(-516.76, -10.24) * mm});
            skLineSegment(sketch, "E390", {"start": v(-516.76, -10.24) * mm, "end": v(-516.76, -54.12) * mm});
            skLineSegment(sketch, "E391", {"start": v(-516.76, -54.12) * mm, "end": v(-516.63, -57.1) * mm});
            skLineSegment(sketch, "E392", {"start": v(-516.63, -57.1) * mm, "end": v(-514.16, -59.58) * mm});
            skLineSegment(sketch, "E393", {"start": v(-514.16, -59.58) * mm, "end": v(-510.05, -59.8) * mm});
            skLineSegment(sketch, "E394", {"start": v(-510.05, -59.8) * mm, "end": v(-470.3, -59.81) * mm});
            skLineSegment(sketch, "E395", {"start": v(-470.3, -59.81) * mm, "end": v(-466.55, -59.9) * mm});
            skLineSegment(sketch, "E396", {"start": v(-466.55, -59.9) * mm, "end": v(-464.29, -60.46) * mm});
            skLineSegment(sketch, "E397", {"start": v(-464.29, -60.46) * mm, "end": v(-464.74, -62.79) * mm});
            skLineSegment(sketch, "E398", {"start": v(-464.74, -62.79) * mm, "end": v(-472.81, -86.14) * mm});
            skLineSegment(sketch, "E399", {"start": v(-472.81, -86.14) * mm, "end": v(-476.67, -88.89) * mm});
            skLineSegment(sketch, "E400", {"start": v(-476.67, -88.89) * mm, "end": v(-479.67, -88.9) * mm});
            skLineSegment(sketch, "E401", {"start": v(-479.67, -88.9) * mm, "end": v(-537.42, -88.89) * mm});
            skLineSegment(sketch, "E402", {"start": v(-537.42, -88.89) * mm, "end": v(-543.4, -88.54) * mm});
            skLineSegment(sketch, "E403", {"start": v(-543.4, -88.54) * mm, "end": v(-556.23, -75.42) * mm});
            skLineSegment(sketch, "E404", {"start": v(-556.23, -75.42) * mm, "end": v(-556.29, -72.42) * mm});
            skLineSegment(sketch, "E405", {"start": v(-556.29, -72.42) * mm, "end": v(-556.29, 9.33) * mm});
            skLineSegment(sketch, "E406", {"start": v(-556.29, 9.33) * mm, "end": v(-555.68, 15.27) * mm});
            skLineSegment(sketch, "E407", {"start": v(-555.68, 15.27) * mm, "end": v(-544.56, 24.58) * mm});
            skLineSegment(sketch, "E408", {"start": v(-544.56, 24.58) * mm, "end": v(-535.2, 24.98) * mm});
            skLineSegment(sketch, "E409", {"start": v(-535.2, 24.98) * mm, "end": v(-523.96, 24.98) * mm});
            skLineSegment(sketch, "E410", {"start": v(-523.96, 24.98) * mm, "end": v(-519.26, 24.59) * mm});
            skLineSegment(sketch, "E411", {"start": v(128.16, 21.5) * mm, "end": v(132.38, 21.83) * mm});
            skLineSegment(sketch, "E412", {"start": v(132.38, 21.83) * mm, "end": v(214.1, 21.83) * mm});
            skLineSegment(sketch, "E413", {"start": v(214.1, 21.83) * mm, "end": v(218.5, 21.08) * mm});
            skLineSegment(sketch, "E414", {"start": v(218.5, 21.08) * mm, "end": v(218.12, 19.34) * mm});
            skLineSegment(sketch, "E415", {"start": v(218.12, 19.34) * mm, "end": v(208.49, -4.28) * mm});
            skLineSegment(sketch, "E416", {"start": v(208.49, -4.28) * mm, "end": v(208.02, -5.27) * mm});
            skLineSegment(sketch, "E417", {"start": v(208.02, -5.27) * mm, "end": v(206.03, -6.63) * mm});
            skLineSegment(sketch, "E418", {"start": v(206.03, -6.63) * mm, "end": v(203.11, -6.7) * mm});
            skLineSegment(sketch, "E419", {"start": v(203.11, -6.7) * mm, "end": v(190.34, -6.71) * mm});
            skLineSegment(sketch, "E420", {"start": v(190.34, -6.71) * mm, "end": v(186.98, -6.95) * mm});
            skLineSegment(sketch, "E421", {"start": v(186.98, -6.95) * mm, "end": v(186.66, -9.23) * mm});
            skLineSegment(sketch, "E422", {"start": v(186.66, -9.23) * mm, "end": v(186.64, -12.51) * mm});
            skLineSegment(sketch, "E423", {"start": v(186.64, -12.51) * mm, "end": v(186.64, -83.65) * mm});
            skLineSegment(sketch, "E424", {"start": v(186.64, -83.65) * mm, "end": v(186.54, -88.15) * mm});
            skLineSegment(sketch, "E425", {"start": v(186.54, -88.15) * mm, "end": v(184.04, -88.83) * mm});
            skLineSegment(sketch, "E426", {"start": v(184.04, -88.83) * mm, "end": v(180.4, -88.9) * mm});
            skLineSegment(sketch, "E427", {"start": v(180.4, -88.9) * mm, "end": v(153.4, -88.9) * mm});
            skLineSegment(sketch, "E428", {"start": v(153.4, -88.9) * mm, "end": v(148.56, -88.19) * mm});
            skLineSegment(sketch, "E429", {"start": v(148.56, -88.19) * mm, "end": v(148.23, -85.88) * mm});
            skLineSegment(sketch, "E430", {"start": v(148.23, -85.88) * mm, "end": v(148.21, -78.22) * mm});
            skLineSegment(sketch, "E431", {"start": v(148.21, -78.22) * mm, "end": v(148.21, -11.82) * mm});
            skLineSegment(sketch, "E432", {"start": v(148.21, -11.82) * mm, "end": v(148.21, -7.74) * mm});
            skLineSegment(sketch, "E433", {"start": v(148.21, -7.74) * mm, "end": v(144.55, -6.72) * mm});
            skLineSegment(sketch, "E434", {"start": v(144.55, -6.72) * mm, "end": v(122.66, -6.7) * mm});
            skLineSegment(sketch, "E435", {"start": v(122.66, -6.7) * mm, "end": v(119.01, -6.64) * mm});
            skLineSegment(sketch, "E436", {"start": v(119.01, -6.64) * mm, "end": v(117.45, -6.3) * mm});
            skLineSegment(sketch, "E437", {"start": v(117.45, -6.3) * mm, "end": v(117.7, -3.37) * mm});
            skLineSegment(sketch, "E438", {"start": v(117.7, -3.37) * mm, "end": v(124.6, 13.1) * mm});
            skLineSegment(sketch, "E439", {"start": v(124.6, 13.1) * mm, "end": v(128.16, 21.5) * mm});
            skLineSegment(sketch, "E440", {"start": v(352.39, -169.95) * mm, "end": v(352.8, -168.77) * mm});
            skLineSegment(sketch, "E441", {"start": v(352.8, -168.77) * mm, "end": v(354.02, -165.64) * mm});
            skLineSegment(sketch, "E442", {"start": v(354.02, -165.64) * mm, "end": v(356.07, -164.29) * mm});
            skLineSegment(sketch, "E443", {"start": v(356.07, -164.29) * mm, "end": v(357.82, -164.29) * mm});
            skLineSegment(sketch, "E444", {"start": v(357.82, -164.29) * mm, "end": v(364.67, -164.29) * mm});
            skLineSegment(sketch, "E445", {"start": v(364.67, -164.29) * mm, "end": v(365.75, -164.25) * mm});
            skLineSegment(sketch, "E446", {"start": v(365.75, -164.25) * mm, "end": v(366.28, -163.73) * mm});
            skLineSegment(sketch, "E447", {"start": v(366.28, -163.73) * mm, "end": v(366.31, -163.06) * mm});
            skLineSegment(sketch, "E448", {"start": v(366.31, -163.06) * mm, "end": v(365.64, -162.18) * mm});
            skLineSegment(sketch, "E449", {"start": v(365.64, -162.18) * mm, "end": v(364.45, -162.06) * mm});
            skLineSegment(sketch, "E450", {"start": v(364.45, -162.06) * mm, "end": v(355.04, -162.06) * mm});
            skLineSegment(sketch, "E451", {"start": v(355.04, -162.06) * mm, "end": v(353.97, -162.04) * mm});
            skLineSegment(sketch, "E452", {"start": v(353.97, -162.04) * mm, "end": v(352.4, -160.65) * mm});
            skLineSegment(sketch, "E453", {"start": v(352.4, -160.65) * mm, "end": v(352.37, -157.02) * mm});
            skLineSegment(sketch, "E454", {"start": v(352.37, -157.02) * mm, "end": v(352.9, -156.3) * mm});
            skLineSegment(sketch, "E455", {"start": v(352.9, -156.3) * mm, "end": v(355, -154.85) * mm});
            skLineSegment(sketch, "E456", {"start": v(355, -154.85) * mm, "end": v(355.82, -154.28) * mm});
            skLineSegment(sketch, "E457", {"start": v(355.82, -154.28) * mm, "end": v(355.5, -153.88) * mm});
            skLineSegment(sketch, "E458", {"start": v(355.5, -153.88) * mm, "end": v(354.96, -153.85) * mm});
            skLineSegment(sketch, "E459", {"start": v(354.96, -153.85) * mm, "end": v(352.34, -151.04) * mm});
            skLineSegment(sketch, "E460", {"start": v(352.34, -151.04) * mm, "end": v(352.33, -147.81) * mm});
            skLineSegment(sketch, "E461", {"start": v(352.33, -147.81) * mm, "end": v(352.33, -143.92) * mm});
            skLineSegment(sketch, "E462", {"start": v(352.33, -143.92) * mm, "end": v(352.34, -143.11) * mm});
            skLineSegment(sketch, "E463", {"start": v(352.34, -143.11) * mm, "end": v(354.44, -140.9) * mm});
            skLineSegment(sketch, "E464", {"start": v(354.44, -140.9) * mm, "end": v(356.58, -140.75) * mm});
            skLineSegment(sketch, "E465", {"start": v(356.58, -140.75) * mm, "end": v(373.92, -140.75) * mm});
            skLineSegment(sketch, "E466", {"start": v(373.92, -140.75) * mm, "end": v(375.12, -140.8) * mm});
            skLineSegment(sketch, "E467", {"start": v(375.12, -140.8) * mm, "end": v(375.8, -141.5) * mm});
            skLineSegment(sketch, "E468", {"start": v(375.8, -141.5) * mm, "end": v(375.83, -142.44) * mm});
            skLineSegment(sketch, "E469", {"start": v(375.83, -142.44) * mm, "end": v(375.82, -149.84) * mm});
            skLineSegment(sketch, "E470", {"start": v(375.82, -149.84) * mm, "end": v(375.62, -151.7) * mm});
            skLineSegment(sketch, "E471", {"start": v(375.62, -151.7) * mm, "end": v(373.56, -153.71) * mm});
            skLineSegment(sketch, "E472", {"start": v(373.56, -153.71) * mm, "end": v(371.69, -153.85) * mm});
            skLineSegment(sketch, "E473", {"start": v(371.69, -153.85) * mm, "end": v(364.63, -153.86) * mm});
            skLineSegment(sketch, "E474", {"start": v(360.4, -153.86) * mm, "end": v(359.06, -153.95) * mm});
            skLineSegment(sketch, "E475", {"start": v(359.06, -153.95) * mm, "end": v(358.58, -154.34) * mm});
            skLineSegment(sketch, "E476", {"start": v(358.58, -154.34) * mm, "end": v(358.62, -155.78) * mm});
            skLineSegment(sketch, "E477", {"start": v(358.62, -155.78) * mm, "end": v(359.1, -156.16) * mm});
            skLineSegment(sketch, "E478", {"start": v(359.1, -156.16) * mm, "end": v(360.18, -156.2) * mm});
            skLineSegment(sketch, "E479", {"start": v(360.18, -156.2) * mm, "end": v(371.87, -156.21) * mm});
            skLineSegment(sketch, "E480", {"start": v(371.87, -156.21) * mm, "end": v(373.08, -156.23) * mm});
            skLineSegment(sketch, "E481", {"start": v(373.08, -156.23) * mm, "end": v(375.6, -158.43) * mm});
            skLineSegment(sketch, "E482", {"start": v(375.6, -158.43) * mm, "end": v(375.82, -160.56) * mm});
            skLineSegment(sketch, "E483", {"start": v(375.82, -160.56) * mm, "end": v(375.82, -165.67) * mm});
            skLineSegment(sketch, "E484", {"start": v(375.82, -165.67) * mm, "end": v(375.61, -167.8) * mm});
            skLineSegment(sketch, "E485", {"start": v(375.61, -167.8) * mm, "end": v(373.17, -170.13) * mm});
            skLineSegment(sketch, "E486", {"start": v(373.17, -170.13) * mm, "end": v(371.43, -170.26) * mm});
            skLineSegment(sketch, "E487", {"start": v(371.43, -170.26) * mm, "end": v(354.1, -170.26) * mm});
            skLineSegment(sketch, "E488", {"start": v(354.1, -170.26) * mm, "end": v(352.39, -169.95) * mm});
            skLineSegment(sketch, "E489", {"start": v(361.98, -145.82) * mm, "end": v(362.05, -148.9) * mm});
            skLineSegment(sketch, "E490", {"start": v(362.05, -148.9) * mm, "end": v(363.91, -148.94) * mm});
            skLineSegment(sketch, "E491", {"start": v(365.65, -148.98) * mm, "end": v(366.3, -148.1) * mm});
            skLineSegment(sketch, "E492", {"start": v(366.3, -148.1) * mm, "end": v(366.31, -144.62) * mm});
            skLineSegment(sketch, "E493", {"start": v(366.31, -144.62) * mm, "end": v(366.18, -143.46) * mm});
            skLineSegment(sketch, "E494", {"start": v(366.18, -143.46) * mm, "end": v(365.74, -144.22) * mm});
            skLineSegment(sketch, "E495", {"start": v(365.74, -144.22) * mm, "end": v(363.55, -145.53) * mm});
            skLineSegment(sketch, "E496", {"start": v(363.55, -145.53) * mm, "end": v(361.98, -145.82) * mm});
            skLineSegment(sketch, "E497", {"start": v(556.2, -141.02) * mm, "end": v(556.29, -142.39) * mm});
            skLineSegment(sketch, "E498", {"start": v(556.29, -142.39) * mm, "end": v(556.28, -149.51) * mm});
            skLineSegment(sketch, "E499", {"start": v(556.28, -149.51) * mm, "end": v(556.08, -151.65) * mm});
            skLineSegment(sketch, "E500", {"start": v(556.08, -151.65) * mm, "end": v(554.06, -153.7) * mm});
            skLineSegment(sketch, "E501", {"start": v(554.06, -153.7) * mm, "end": v(552.2, -153.85) * mm});
            skLineSegment(sketch, "E502", {"start": v(552.2, -153.85) * mm, "end": v(544.87, -153.86) * mm});
            skLineSegment(sketch, "E503", {"start": v(541.17, -153.86) * mm, "end": v(540.1, -153.87) * mm});
            skLineSegment(sketch, "E504", {"start": v(540.1, -153.87) * mm, "end": v(539.05, -154.3) * mm});
            skLineSegment(sketch, "E505", {"start": v(539.05, -154.3) * mm, "end": v(539.12, -155.86) * mm});
            skLineSegment(sketch, "E506", {"start": v(539.12, -155.86) * mm, "end": v(539.65, -156.18) * mm});
            skLineSegment(sketch, "E507", {"start": v(539.65, -156.18) * mm, "end": v(540.73, -156.2) * mm});
            skLineSegment(sketch, "E508", {"start": v(540.73, -156.2) * mm, "end": v(552.28, -156.21) * mm});
            skLineSegment(sketch, "E509", {"start": v(552.28, -156.21) * mm, "end": v(553.5, -156.22) * mm});
            skLineSegment(sketch, "E510", {"start": v(553.5, -156.22) * mm, "end": v(556.1, -158.66) * mm});
            skLineSegment(sketch, "E511", {"start": v(556.1, -158.66) * mm, "end": v(556.25, -159.86) * mm});
            skLineSegment(sketch, "E512", {"start": v(556.25, -159.86) * mm, "end": v(556.1, -167.5) * mm});
            skLineSegment(sketch, "E513", {"start": v(556.1, -167.5) * mm, "end": v(553.52, -170.14) * mm});
            skLineSegment(sketch, "E514", {"start": v(553.52, -170.14) * mm, "end": v(552.05, -170.26) * mm});
            skLineSegment(sketch, "E515", {"start": v(552.05, -170.26) * mm, "end": v(534.44, -170.26) * mm});
            skLineSegment(sketch, "E516", {"start": v(534.44, -170.26) * mm, "end": v(532.92, -169.97) * mm});
            skLineSegment(sketch, "E517", {"start": v(532.92, -169.97) * mm, "end": v(535.22, -164.33) * mm});
            skLineSegment(sketch, "E518", {"start": v(535.22, -164.33) * mm, "end": v(536.63, -164.3) * mm});
            skLineSegment(sketch, "E519", {"start": v(536.63, -164.3) * mm, "end": v(544.96, -164.29) * mm});
            skLineSegment(sketch, "E520", {"start": v(544.96, -164.29) * mm, "end": v(545.63, -164.3) * mm});
            skLineSegment(sketch, "E521", {"start": v(545.63, -164.3) * mm, "end": v(546.7, -162.7) * mm});
            skLineSegment(sketch, "E522", {"start": v(546.7, -162.7) * mm, "end": v(546.24, -162.26) * mm});
            skLineSegment(sketch, "E523", {"start": v(546.24, -162.26) * mm, "end": v(544.93, -162.07) * mm});
            skLineSegment(sketch, "E524", {"start": v(544.93, -162.07) * mm, "end": v(535.52, -162.06) * mm});
            skLineSegment(sketch, "E525", {"start": v(535.52, -162.06) * mm, "end": v(534.44, -162.04) * mm});
            skLineSegment(sketch, "E526", {"start": v(534.44, -162.04) * mm, "end": v(532.84, -160.54) * mm});
            skLineSegment(sketch, "E527", {"start": v(532.84, -160.54) * mm, "end": v(532.82, -157.05) * mm});
            skLineSegment(sketch, "E528", {"start": v(532.82, -157.05) * mm, "end": v(533.33, -156.3) * mm});
            skLineSegment(sketch, "E529", {"start": v(533.33, -156.3) * mm, "end": v(535.88, -154.55) * mm});
            skLineSegment(sketch, "E530", {"start": v(535.88, -154.55) * mm, "end": v(536.36, -154.13) * mm});
            skLineSegment(sketch, "E531", {"start": v(536.36, -154.13) * mm, "end": v(535.3, -153.85) * mm});
            skLineSegment(sketch, "E532", {"start": v(535.3, -153.85) * mm, "end": v(532.8, -151.08) * mm});
            skLineSegment(sketch, "E533", {"start": v(532.8, -151.08) * mm, "end": v(532.8, -143.42) * mm});
            skLineSegment(sketch, "E534", {"start": v(532.8, -143.42) * mm, "end": v(532.82, -142.88) * mm});
            skLineSegment(sketch, "E535", {"start": v(532.82, -142.88) * mm, "end": v(534.71, -140.91) * mm});
            skLineSegment(sketch, "E536", {"start": v(534.71, -140.91) * mm, "end": v(536.99, -140.75) * mm});
            skLineSegment(sketch, "E537", {"start": v(536.99, -140.75) * mm, "end": v(554.46, -140.75) * mm});
            skLineSegment(sketch, "E538", {"start": v(554.46, -140.75) * mm, "end": v(556.2, -141.02) * mm});
            skLineSegment(sketch, "E539", {"start": v(546.77, -143.58) * mm, "end": v(546.52, -143.54) * mm});
            skLineSegment(sketch, "E540", {"start": v(546.52, -143.54) * mm, "end": v(545.91, -144.71) * mm});
            skLineSegment(sketch, "E541", {"start": v(545.91, -144.71) * mm, "end": v(544.65, -145.5) * mm});
            skLineSegment(sketch, "E542", {"start": v(544.65, -145.5) * mm, "end": v(543.32, -145.55) * mm});
            skLineSegment(sketch, "E543", {"start": v(543.32, -145.55) * mm, "end": v(542.4, -145.79) * mm});
            skLineSegment(sketch, "E544", {"start": v(542.4, -145.79) * mm, "end": v(542.35, -148.36) * mm});
            skLineSegment(sketch, "E545", {"start": v(542.35, -148.36) * mm, "end": v(543.05, -149.02) * mm});
            skLineSegment(sketch, "E546", {"start": v(543.05, -149.02) * mm, "end": v(544.1, -149.03) * mm});
            skLineSegment(sketch, "E547", {"start": v(545.84, -149.03) * mm, "end": v(546.76, -148.08) * mm});
            skLineSegment(sketch, "E548", {"start": v(546.76, -148.08) * mm, "end": v(546.77, -143.58) * mm});
            skLineSegment(sketch, "E549", {"start": v(298.67, -140.35) * mm, "end": v(296.55, -140.2) * mm});
            skLineSegment(sketch, "E550", {"start": v(296.55, -140.2) * mm, "end": v(296.72, -139.25) * mm});
            skLineSegment(sketch, "E551", {"start": v(296.72, -139.25) * mm, "end": v(298.94, -133.5) * mm});
            skLineSegment(sketch, "E552", {"start": v(298.94, -133.5) * mm, "end": v(300.24, -132.58) * mm});
            skLineSegment(sketch, "E553", {"start": v(300.24, -132.58) * mm, "end": v(300.92, -132.58) * mm});
            skLineSegment(sketch, "E554", {"start": v(300.92, -132.58) * mm, "end": v(320.54, -132.58) * mm});
            skLineSegment(sketch, "E555", {"start": v(320.54, -132.58) * mm, "end": v(322.08, -132.74) * mm});
            skLineSegment(sketch, "E556", {"start": v(322.08, -132.74) * mm, "end": v(322.07, -133.5) * mm});
            skLineSegment(sketch, "E557", {"start": v(322.07, -133.5) * mm, "end": v(319.9, -139.78) * mm});
            skLineSegment(sketch, "E558", {"start": v(319.9, -139.78) * mm, "end": v(318.15, -140.14) * mm});
            skLineSegment(sketch, "E559", {"start": v(318.15, -140.14) * mm, "end": v(310.9, -140.15) * mm});
            skLineSegment(sketch, "E560", {"start": v(310.9, -140.15) * mm, "end": v(309.39, -140.22) * mm});
            skLineSegment(sketch, "E561", {"start": v(309.39, -140.22) * mm, "end": v(309.22, -141.2) * mm});
            skLineSegment(sketch, "E562", {"start": v(309.22, -141.2) * mm, "end": v(309.21, -147.39) * mm});
            skLineSegment(sketch, "E563", {"start": v(309.21, -147.39) * mm, "end": v(309.6, -146.98) * mm});
            skLineSegment(sketch, "E564", {"start": v(309.6, -146.98) * mm, "end": v(310.67, -144.1) * mm});
            skLineSegment(sketch, "E565", {"start": v(310.67, -144.1) * mm, "end": v(311.47, -143.48) * mm});
            skLineSegment(sketch, "E566", {"start": v(311.47, -143.48) * mm, "end": v(312, -143.44) * mm});
            skLineSegment(sketch, "E567", {"start": v(312, -143.44) * mm, "end": v(320.47, -143.45) * mm});
            skLineSegment(sketch, "E568", {"start": v(320.47, -143.45) * mm, "end": v(321.56, -143.65) * mm});
            skLineSegment(sketch, "E569", {"start": v(321.56, -143.65) * mm, "end": v(321.44, -144.36) * mm});
            skLineSegment(sketch, "E570", {"start": v(321.44, -144.36) * mm, "end": v(319.4, -150.05) * mm});
            skLineSegment(sketch, "E571", {"start": v(319.4, -150.05) * mm, "end": v(318, -151) * mm});
            skLineSegment(sketch, "E572", {"start": v(318, -151) * mm, "end": v(310.87, -151) * mm});
            skLineSegment(sketch, "E573", {"start": v(310.87, -151) * mm, "end": v(309.37, -151.17) * mm});
            skLineSegment(sketch, "E574", {"start": v(309.37, -151.17) * mm, "end": v(309.22, -152.7) * mm});
            skLineSegment(sketch, "E575", {"start": v(309.22, -152.7) * mm, "end": v(309.38, -154.2) * mm});
            skLineSegment(sketch, "E576", {"start": v(309.38, -154.2) * mm, "end": v(310.79, -154.36) * mm});
            skLineSegment(sketch, "E577", {"start": v(310.79, -154.36) * mm, "end": v(320.46, -154.37) * mm});
            skLineSegment(sketch, "E578", {"start": v(320.46, -154.37) * mm, "end": v(321.94, -154.58) * mm});
            skLineSegment(sketch, "E579", {"start": v(321.94, -154.58) * mm, "end": v(321.32, -157) * mm});
            skLineSegment(sketch, "E580", {"start": v(321.32, -157) * mm, "end": v(320.46, -159.54) * mm});
            skLineSegment(sketch, "E581", {"start": v(320.46, -159.54) * mm, "end": v(319.57, -161.96) * mm});
            skLineSegment(sketch, "E582", {"start": v(319.57, -161.96) * mm, "end": v(318.47, -162.05) * mm});
            skLineSegment(sketch, "E583", {"start": v(318.47, -162.05) * mm, "end": v(300.2, -162.05) * mm});
            skLineSegment(sketch, "E584", {"start": v(300.2, -162.05) * mm, "end": v(299.19, -161.98) * mm});
            skLineSegment(sketch, "E585", {"start": v(299.19, -161.98) * mm, "end": v(298.9, -160.07) * mm});
            skLineSegment(sketch, "E586", {"start": v(298.9, -160.07) * mm, "end": v(298.89, -142.06) * mm});
            skLineSegment(sketch, "E587", {"start": v(298.89, -142.06) * mm, "end": v(298.67, -140.35) * mm});
            skLineSegment(sketch, "E588", {"start": v(392.54, -146.82) * mm, "end": v(390.92, -146.6) * mm});
            skLineSegment(sketch, "E589", {"start": v(390.92, -146.6) * mm, "end": v(390.93, -146) * mm});
            skLineSegment(sketch, "E590", {"start": v(390.93, -146) * mm, "end": v(392.62, -141.47) * mm});
            skLineSegment(sketch, "E591", {"start": v(392.62, -141.47) * mm, "end": v(393.51, -140.78) * mm});
            skLineSegment(sketch, "E592", {"start": v(393.51, -140.78) * mm, "end": v(394.45, -140.75) * mm});
            skLineSegment(sketch, "E593", {"start": v(394.45, -140.75) * mm, "end": v(400.23, -140.75) * mm});
            skLineSegment(sketch, "E594", {"start": v(400.23, -140.75) * mm, "end": v(401.82, -141.04) * mm});
            skLineSegment(sketch, "E595", {"start": v(401.82, -141.04) * mm, "end": v(402.04, -144.13) * mm});
            skLineSegment(sketch, "E596", {"start": v(402.04, -144.13) * mm, "end": v(402.4, -143.35) * mm});
            skLineSegment(sketch, "E597", {"start": v(402.4, -143.35) * mm, "end": v(403.09, -141.6) * mm});
            skLineSegment(sketch, "E598", {"start": v(403.09, -141.6) * mm, "end": v(404.3, -140.76) * mm});
            skLineSegment(sketch, "E599", {"start": v(404.3, -140.76) * mm, "end": v(405.1, -140.75) * mm});
            skLineSegment(sketch, "E600", {"start": v(405.1, -140.75) * mm, "end": v(411.15, -140.75) * mm});
            skLineSegment(sketch, "E601", {"start": v(411.15, -140.75) * mm, "end": v(413.43, -140.9) * mm});
            skLineSegment(sketch, "E602", {"start": v(413.43, -140.9) * mm, "end": v(415.93, -143.19) * mm});
            skLineSegment(sketch, "E603", {"start": v(415.93, -143.19) * mm, "end": v(416.16, -145.18) * mm});
            skLineSegment(sketch, "E604", {"start": v(416.16, -145.18) * mm, "end": v(416.17, -160.51) * mm});
            skLineSegment(sketch, "E605", {"start": v(416.17, -160.51) * mm, "end": v(415.9, -161.92) * mm});
            skLineSegment(sketch, "E606", {"start": v(415.9, -161.92) * mm, "end": v(406.9, -161.93) * mm});
            skLineSegment(sketch, "E607", {"start": v(406.9, -161.93) * mm, "end": v(406.67, -160.53) * mm});
            skLineSegment(sketch, "E608", {"start": v(406.67, -160.53) * mm, "end": v(406.66, -148.7) * mm});
            skLineSegment(sketch, "E609", {"start": v(406.66, -148.7) * mm, "end": v(406.65, -147.62) * mm});
            skLineSegment(sketch, "E610", {"start": v(406.65, -147.62) * mm, "end": v(405.74, -146.73) * mm});
            skLineSegment(sketch, "E611", {"start": v(405.74, -146.73) * mm, "end": v(403.19, -146.73) * mm});
            skLineSegment(sketch, "E612", {"start": v(403.19, -146.73) * mm, "end": v(402.28, -147.66) * mm});
            skLineSegment(sketch, "E613", {"start": v(402.28, -147.66) * mm, "end": v(402.27, -148.73) * mm});
            skLineSegment(sketch, "E614", {"start": v(402.27, -148.73) * mm, "end": v(402.26, -160.43) * mm});
            skLineSegment(sketch, "E615", {"start": v(402.26, -160.43) * mm, "end": v(402.1, -161.95) * mm});
            skLineSegment(sketch, "E616", {"start": v(402.1, -161.95) * mm, "end": v(399.04, -162.05) * mm});
            skLineSegment(sketch, "E617", {"start": v(399.04, -162.05) * mm, "end": v(396.08, -162.05) * mm});
            skLineSegment(sketch, "E618", {"start": v(396.08, -162.05) * mm, "end": v(393.04, -161.95) * mm});
            skLineSegment(sketch, "E619", {"start": v(393.04, -161.95) * mm, "end": v(392.76, -160.2) * mm});
            skLineSegment(sketch, "E620", {"start": v(392.76, -160.2) * mm, "end": v(392.75, -148.51) * mm});
            skLineSegment(sketch, "E621", {"start": v(392.75, -148.51) * mm, "end": v(392.54, -146.82) * mm});
            skLineSegment(sketch, "E622", {"start": v(529.12, -161.87) * mm, "end": v(528.62, -162.03) * mm});
            skLineSegment(sketch, "E623", {"start": v(528.62, -162.03) * mm, "end": v(520.83, -162.05) * mm});
            skLineSegment(sketch, "E624", {"start": v(520.83, -162.05) * mm, "end": v(519.96, -162) * mm});
            skLineSegment(sketch, "E625", {"start": v(519.96, -162) * mm, "end": v(519.72, -161.11) * mm});
            skLineSegment(sketch, "E626", {"start": v(519.72, -161.11) * mm, "end": v(519.7, -159.9) * mm});
            skLineSegment(sketch, "E627", {"start": v(519.7, -159.9) * mm, "end": v(519.7, -148.75) * mm});
            skLineSegment(sketch, "E628", {"start": v(519.7, -148.75) * mm, "end": v(519.65, -147.4) * mm});
            skLineSegment(sketch, "E629", {"start": v(519.65, -147.4) * mm, "end": v(518.95, -146.74) * mm});
            skLineSegment(sketch, "E630", {"start": v(518.95, -146.74) * mm, "end": v(516.26, -146.73) * mm});
            skLineSegment(sketch, "E631", {"start": v(516.26, -146.73) * mm, "end": v(515.45, -147.45) * mm});
            skLineSegment(sketch, "E632", {"start": v(515.45, -147.45) * mm, "end": v(515.41, -148.66) * mm});
            skLineSegment(sketch, "E633", {"start": v(515.41, -148.66) * mm, "end": v(515.4, -160.21) * mm});
            skLineSegment(sketch, "E634", {"start": v(515.4, -160.21) * mm, "end": v(515.13, -161.95) * mm});
            skLineSegment(sketch, "E635", {"start": v(515.13, -161.95) * mm, "end": v(514.5, -162.05) * mm});
            skLineSegment(sketch, "E636", {"start": v(514.5, -162.05) * mm, "end": v(506.44, -162.03) * mm});
            skLineSegment(sketch, "E637", {"start": v(506.44, -162.03) * mm, "end": v(506.05, -161.88) * mm});
            skLineSegment(sketch, "E638", {"start": v(506.05, -161.88) * mm, "end": v(505.9, -160.44) * mm});
            skLineSegment(sketch, "E639", {"start": v(505.9, -160.44) * mm, "end": v(505.9, -148.34) * mm});
            skLineSegment(sketch, "E640", {"start": v(505.9, -148.34) * mm, "end": v(505.77, -146.83) * mm});
            skLineSegment(sketch, "E641", {"start": v(505.77, -146.83) * mm, "end": v(504, -146.61) * mm});
            skLineSegment(sketch, "E642", {"start": v(504, -146.61) * mm, "end": v(504.07, -145.8) * mm});
            skLineSegment(sketch, "E643", {"start": v(504.07, -145.8) * mm, "end": v(505.67, -141.52) * mm});
            skLineSegment(sketch, "E644", {"start": v(505.67, -141.52) * mm, "end": v(506.66, -140.78) * mm});
            skLineSegment(sketch, "E645", {"start": v(506.66, -140.78) * mm, "end": v(507.47, -140.75) * mm});
            skLineSegment(sketch, "E646", {"start": v(507.47, -140.75) * mm, "end": v(513.38, -140.75) * mm});
            skLineSegment(sketch, "E647", {"start": v(513.38, -140.75) * mm, "end": v(514.86, -141) * mm});
            skLineSegment(sketch, "E648", {"start": v(514.86, -141) * mm, "end": v(515.03, -143.9) * mm});
            skLineSegment(sketch, "E649", {"start": v(515.03, -143.9) * mm, "end": v(515.36, -143.62) * mm});
            skLineSegment(sketch, "E650", {"start": v(515.36, -143.62) * mm, "end": v(516.4, -141.1) * mm});
            skLineSegment(sketch, "E651", {"start": v(516.4, -141.1) * mm, "end": v(517.89, -140.75) * mm});
            skLineSegment(sketch, "E652", {"start": v(517.89, -140.75) * mm, "end": v(524.6, -140.75) * mm});
            skLineSegment(sketch, "E653", {"start": v(524.6, -140.75) * mm, "end": v(526.48, -140.9) * mm});
            skLineSegment(sketch, "E654", {"start": v(526.48, -140.9) * mm, "end": v(528.95, -143.04) * mm});
            skLineSegment(sketch, "E655", {"start": v(528.95, -143.04) * mm, "end": v(529.2, -144.62) * mm});
            skLineSegment(sketch, "E656", {"start": v(529.2, -144.62) * mm, "end": v(529.2, -160.88) * mm});
            skLineSegment(sketch, "E657", {"start": v(529.2, -160.88) * mm, "end": v(529.12, -161.87) * mm});
            skLineSegment(sketch, "E658", {"start": v(334.7, -161.93) * mm, "end": v(334.2, -162.04) * mm});
            skLineSegment(sketch, "E659", {"start": v(334.2, -162.04) * mm, "end": v(326.14, -162.04) * mm});
            skLineSegment(sketch, "E660", {"start": v(326.14, -162.04) * mm, "end": v(325.62, -161.93) * mm});
            skLineSegment(sketch, "E661", {"start": v(325.62, -161.93) * mm, "end": v(325.44, -160.46) * mm});
            skLineSegment(sketch, "E662", {"start": v(325.44, -160.46) * mm, "end": v(325.44, -148.36) * mm});
            skLineSegment(sketch, "E663", {"start": v(325.44, -148.36) * mm, "end": v(325.3, -146.83) * mm});
            skLineSegment(sketch, "E664", {"start": v(325.3, -146.83) * mm, "end": v(323.53, -146.6) * mm});
            skLineSegment(sketch, "E665", {"start": v(323.53, -146.6) * mm, "end": v(323.65, -145.68) * mm});
            skLineSegment(sketch, "E666", {"start": v(323.65, -145.68) * mm, "end": v(325.16, -141.66) * mm});
            skLineSegment(sketch, "E667", {"start": v(325.16, -141.66) * mm, "end": v(326.34, -140.76) * mm});
            skLineSegment(sketch, "E668", {"start": v(326.34, -140.76) * mm, "end": v(333.6, -140.77) * mm});
            skLineSegment(sketch, "E669", {"start": v(333.6, -140.77) * mm, "end": v(334.39, -140.95) * mm});
            skLineSegment(sketch, "E670", {"start": v(334.39, -140.95) * mm, "end": v(334.56, -144.09) * mm});
            skLineSegment(sketch, "E671", {"start": v(334.56, -144.09) * mm, "end": v(334.95, -143.54) * mm});
            skLineSegment(sketch, "E672", {"start": v(334.95, -143.54) * mm, "end": v(336.11, -140.88) * mm});
            skLineSegment(sketch, "E673", {"start": v(336.11, -140.88) * mm, "end": v(337.53, -140.75) * mm});
            skLineSegment(sketch, "E674", {"start": v(337.53, -140.75) * mm, "end": v(343.98, -140.75) * mm});
            skLineSegment(sketch, "E675", {"start": v(343.98, -140.75) * mm, "end": v(346.12, -140.92) * mm});
            skLineSegment(sketch, "E676", {"start": v(346.12, -140.92) * mm, "end": v(348.45, -142.87) * mm});
            skLineSegment(sketch, "E677", {"start": v(348.45, -142.87) * mm, "end": v(348.73, -144.44) * mm});
            skLineSegment(sketch, "E678", {"start": v(348.73, -144.44) * mm, "end": v(348.74, -161.11) * mm});
            skLineSegment(sketch, "E679", {"start": v(348.74, -161.11) * mm, "end": v(348.66, -161.83) * mm});
            skLineSegment(sketch, "E680", {"start": v(348.66, -161.83) * mm, "end": v(348.06, -162.03) * mm});
            skLineSegment(sketch, "E681", {"start": v(348.06, -162.03) * mm, "end": v(339.87, -162.03) * mm});
            skLineSegment(sketch, "E682", {"start": v(339.87, -162.03) * mm, "end": v(339.5, -161.92) * mm});
            skLineSegment(sketch, "E683", {"start": v(339.5, -161.92) * mm, "end": v(339.24, -160.2) * mm});
            skLineSegment(sketch, "E684", {"start": v(339.24, -160.2) * mm, "end": v(339.23, -148.65) * mm});
            skLineSegment(sketch, "E685", {"start": v(339.23, -148.65) * mm, "end": v(339.2, -147.44) * mm});
            skLineSegment(sketch, "E686", {"start": v(339.2, -147.44) * mm, "end": v(338.52, -146.75) * mm});
            skLineSegment(sketch, "E687", {"start": v(338.52, -146.75) * mm, "end": v(335.7, -146.75) * mm});
            skLineSegment(sketch, "E688", {"start": v(335.7, -146.75) * mm, "end": v(335, -147.42) * mm});
            skLineSegment(sketch, "E689", {"start": v(335, -147.42) * mm, "end": v(334.95, -148.76) * mm});
            skLineSegment(sketch, "E690", {"start": v(334.95, -148.76) * mm, "end": v(334.95, -160.2) * mm});
            skLineSegment(sketch, "E691", {"start": v(334.95, -160.2) * mm, "end": v(334.7, -161.93) * mm});
            skLineSegment(sketch, "E692", {"start": v(442.25, -152.9) * mm, "end": v(435.67, -152.91) * mm});
            skLineSegment(sketch, "E693", {"start": v(435.67, -152.91) * mm, "end": v(431.41, -152.93) * mm});
            skLineSegment(sketch, "E694", {"start": v(429.34, -152.93) * mm, "end": v(429.24, -155.53) * mm});
            skLineSegment(sketch, "E695", {"start": v(429.24, -155.53) * mm, "end": v(430, -156.2) * mm});
            skLineSegment(sketch, "E696", {"start": v(430, -156.2) * mm, "end": v(431.07, -156.2) * mm});
            skLineSegment(sketch, "E697", {"start": v(431.07, -156.2) * mm, "end": v(440.75, -156.22) * mm});
            skLineSegment(sketch, "E698", {"start": v(440.75, -156.22) * mm, "end": v(442.21, -156.39) * mm});
            skLineSegment(sketch, "E699", {"start": v(442.21, -156.39) * mm, "end": v(442.2, -156.9) * mm});
            skLineSegment(sketch, "E700", {"start": v(442.2, -156.9) * mm, "end": v(440.3, -161.96) * mm});
            skLineSegment(sketch, "E701", {"start": v(440.3, -161.96) * mm, "end": v(439.21, -162.05) * mm});
            skLineSegment(sketch, "E702", {"start": v(439.21, -162.05) * mm, "end": v(423.08, -162.05) * mm});
            skLineSegment(sketch, "E703", {"start": v(423.08, -162.05) * mm, "end": v(419.85, -159.44) * mm});
            skLineSegment(sketch, "E704", {"start": v(419.85, -159.44) * mm, "end": v(419.66, -157.58) * mm});
            skLineSegment(sketch, "E705", {"start": v(419.66, -157.58) * mm, "end": v(419.66, -144.81) * mm});
            skLineSegment(sketch, "E706", {"start": v(419.66, -144.81) * mm, "end": v(419.88, -142.95) * mm});
            skLineSegment(sketch, "E707", {"start": v(419.88, -142.95) * mm, "end": v(422.23, -140.89) * mm});
            skLineSegment(sketch, "E708", {"start": v(422.23, -140.89) * mm, "end": v(424.23, -140.75) * mm});
            skLineSegment(sketch, "E709", {"start": v(424.23, -140.75) * mm, "end": v(437.13, -140.75) * mm});
            skLineSegment(sketch, "E710", {"start": v(437.13, -140.75) * mm, "end": v(439.68, -140.9) * mm});
            skLineSegment(sketch, "E711", {"start": v(439.68, -140.9) * mm, "end": v(442.33, -143.62) * mm});
            skLineSegment(sketch, "E712", {"start": v(442.33, -143.62) * mm, "end": v(442.37, -144.3) * mm});
            skLineSegment(sketch, "E713", {"start": v(442.37, -144.3) * mm, "end": v(442.37, -151.82) * mm});
            skLineSegment(sketch, "E714", {"start": v(442.37, -151.82) * mm, "end": v(442.25, -152.9) * mm});
            skLineSegment(sketch, "E715", {"start": v(429.17, -149.87) * mm, "end": v(429.39, -149.92) * mm});
            skLineSegment(sketch, "E716", {"start": v(429.39, -149.92) * mm, "end": v(430.07, -148.78) * mm});
            skLineSegment(sketch, "E717", {"start": v(430.07, -148.78) * mm, "end": v(430.9, -148.29) * mm});
            skLineSegment(sketch, "E718", {"start": v(431.4, -148.02) * mm, "end": v(431.76, -148) * mm});
            skLineSegment(sketch, "E719", {"start": v(431.76, -148) * mm, "end": v(432.98, -146.72) * mm});
            skLineSegment(sketch, "E720", {"start": v(432.98, -146.72) * mm, "end": v(432.92, -146.06) * mm});
            skLineSegment(sketch, "E721", {"start": v(432.92, -146.06) * mm, "end": v(432.18, -145.4) * mm});
            skLineSegment(sketch, "E722", {"start": v(432.18, -145.4) * mm, "end": v(430.05, -145.42) * mm});
            skLineSegment(sketch, "E723", {"start": v(430.05, -145.42) * mm, "end": v(429.17, -146.41) * mm});
            skLineSegment(sketch, "E724", {"start": v(429.17, -146.41) * mm, "end": v(429.17, -149.87) * mm});
            skLineSegment(sketch, "E725", {"start": v(468.64, -152.8) * mm, "end": v(464.25, -152.9) * mm});
            skLineSegment(sketch, "E726", {"start": v(464.25, -152.9) * mm, "end": v(460.08, -152.91) * mm});
            skLineSegment(sketch, "E727", {"start": v(460.08, -152.91) * mm, "end": v(457.95, -152.91) * mm});
            skLineSegment(sketch, "E728", {"start": v(455.77, -152.91) * mm, "end": v(455.6, -155.6) * mm});
            skLineSegment(sketch, "E729", {"start": v(455.6, -155.6) * mm, "end": v(456.27, -156.18) * mm});
            skLineSegment(sketch, "E730", {"start": v(456.27, -156.18) * mm, "end": v(457.34, -156.2) * mm});
            skLineSegment(sketch, "E731", {"start": v(457.34, -156.2) * mm, "end": v(467.02, -156.21) * mm});
            skLineSegment(sketch, "E732", {"start": v(467.02, -156.21) * mm, "end": v(468.55, -156.26) * mm});
            skLineSegment(sketch, "E733", {"start": v(468.55, -156.26) * mm, "end": v(467.7, -159.23) * mm});
            skLineSegment(sketch, "E734", {"start": v(467.7, -159.23) * mm, "end": v(466.58, -161.98) * mm});
            skLineSegment(sketch, "E735", {"start": v(466.58, -161.98) * mm, "end": v(465.49, -162.05) * mm});
            skLineSegment(sketch, "E736", {"start": v(465.49, -162.05) * mm, "end": v(449.5, -162.06) * mm});
            skLineSegment(sketch, "E737", {"start": v(449.5, -162.06) * mm, "end": v(446.18, -159.38) * mm});
            skLineSegment(sketch, "E738", {"start": v(446.18, -159.38) * mm, "end": v(446.02, -157.78) * mm});
            skLineSegment(sketch, "E739", {"start": v(446.02, -157.78) * mm, "end": v(446.02, -144.61) * mm});
            skLineSegment(sketch, "E740", {"start": v(446.02, -144.61) * mm, "end": v(446.24, -142.89) * mm});
            skLineSegment(sketch, "E741", {"start": v(446.24, -142.89) * mm, "end": v(448.5, -140.9) * mm});
            skLineSegment(sketch, "E742", {"start": v(448.5, -140.9) * mm, "end": v(450.37, -140.75) * mm});
            skLineSegment(sketch, "E743", {"start": v(450.37, -140.75) * mm, "end": v(463.8, -140.75) * mm});
            skLineSegment(sketch, "E744", {"start": v(463.8, -140.75) * mm, "end": v(466.08, -140.9) * mm});
            skLineSegment(sketch, "E745", {"start": v(466.08, -140.9) * mm, "end": v(468.66, -143.42) * mm});
            skLineSegment(sketch, "E746", {"start": v(468.66, -143.42) * mm, "end": v(468.72, -144.63) * mm});
            skLineSegment(sketch, "E747", {"start": v(468.72, -144.63) * mm, "end": v(468.73, -151.75) * mm});
            skLineSegment(sketch, "E748", {"start": v(468.73, -151.75) * mm, "end": v(468.64, -152.8) * mm});
            skLineSegment(sketch, "E749", {"start": v(455.53, -150.15) * mm, "end": v(456.04, -149.43) * mm});
            skLineSegment(sketch, "E750", {"start": v(456.04, -149.43) * mm, "end": v(457.46, -148.53) * mm});
            skLineSegment(sketch, "E751", {"start": v(458.31, -147.99) * mm, "end": v(459.32, -146.89) * mm});
            skLineSegment(sketch, "E752", {"start": v(459.32, -146.89) * mm, "end": v(459.13, -145.85) * mm});
            skLineSegment(sketch, "E753", {"start": v(459.13, -145.85) * mm, "end": v(458.66, -145.44) * mm});
            skLineSegment(sketch, "E754", {"start": v(458.66, -145.44) * mm, "end": v(456.25, -145.45) * mm});
            skLineSegment(sketch, "E755", {"start": v(456.25, -145.45) * mm, "end": v(455.54, -146.3) * mm});
            skLineSegment(sketch, "E756", {"start": v(455.54, -146.3) * mm, "end": v(455.53, -150.15) * mm});
            skLineSegment(sketch, "E757", {"start": v(490.76, -140.96) * mm, "end": v(488.62, -146.62) * mm});
            skLineSegment(sketch, "E758", {"start": v(488.62, -146.62) * mm, "end": v(487.63, -146.71) * mm});
            skLineSegment(sketch, "E759", {"start": v(487.63, -146.71) * mm, "end": v(483.73, -146.72) * mm});
            skLineSegment(sketch, "E760", {"start": v(483.73, -146.72) * mm, "end": v(482.93, -146.73) * mm});
            skLineSegment(sketch, "E761", {"start": v(482.93, -146.73) * mm, "end": v(481.9, -147.73) * mm});
            skLineSegment(sketch, "E762", {"start": v(481.9, -147.73) * mm, "end": v(481.88, -148.8) * mm});
            skLineSegment(sketch, "E763", {"start": v(481.88, -148.8) * mm, "end": v(481.87, -160.37) * mm});
            skLineSegment(sketch, "E764", {"start": v(481.87, -160.37) * mm, "end": v(481.82, -161.87) * mm});
            skLineSegment(sketch, "E765", {"start": v(481.82, -161.87) * mm, "end": v(481.13, -162.04) * mm});
            skLineSegment(sketch, "E766", {"start": v(481.13, -162.04) * mm, "end": v(473.06, -162.04) * mm});
            skLineSegment(sketch, "E767", {"start": v(473.06, -162.04) * mm, "end": v(472.7, -161.95) * mm});
            skLineSegment(sketch, "E768", {"start": v(472.7, -161.95) * mm, "end": v(472.37, -160.94) * mm});
            skLineSegment(sketch, "E769", {"start": v(472.37, -160.94) * mm, "end": v(472.36, -158.66) * mm});
            skLineSegment(sketch, "E770", {"start": v(472.36, -158.66) * mm, "end": v(472.36, -148.58) * mm});
            skLineSegment(sketch, "E771", {"start": v(472.36, -148.58) * mm, "end": v(472.32, -147.08) * mm});
            skLineSegment(sketch, "E772", {"start": v(472.32, -147.08) * mm, "end": v(470.57, -146.46) * mm});
            skLineSegment(sketch, "E773", {"start": v(470.57, -146.46) * mm, "end": v(470.68, -145.86) * mm});
            skLineSegment(sketch, "E774", {"start": v(470.68, -145.86) * mm, "end": v(472.76, -140.95) * mm});
            skLineSegment(sketch, "E775", {"start": v(472.76, -140.95) * mm, "end": v(473.47, -140.78) * mm});
            skLineSegment(sketch, "E776", {"start": v(473.47, -140.78) * mm, "end": v(480.6, -140.77) * mm});
            skLineSegment(sketch, "E777", {"start": v(480.6, -140.77) * mm, "end": v(481.35, -140.9) * mm});
            skLineSegment(sketch, "E778", {"start": v(481.35, -140.9) * mm, "end": v(481.6, -142.23) * mm});
            skLineSegment(sketch, "E779", {"start": v(481.6, -142.23) * mm, "end": v(481.6, -143.75) * mm});
            skLineSegment(sketch, "E780", {"start": v(481.6, -143.75) * mm, "end": v(482.86, -140.97) * mm});
            skLineSegment(sketch, "E781", {"start": v(482.86, -140.97) * mm, "end": v(485.47, -140.75) * mm});
            skLineSegment(sketch, "E782", {"start": v(485.47, -140.75) * mm, "end": v(488.02, -140.75) * mm});
            skLineSegment(sketch, "E783", {"start": v(488.02, -140.75) * mm, "end": v(490.76, -140.96) * mm});
            skLineSegment(sketch, "E784", {"start": v(492.82, -140.9) * mm, "end": v(494.25, -140.75) * mm});
            skLineSegment(sketch, "E785", {"start": v(494.25, -140.75) * mm, "end": v(500.7, -140.75) * mm});
            skLineSegment(sketch, "E786", {"start": v(500.7, -140.75) * mm, "end": v(502.23, -142.28) * mm});
            skLineSegment(sketch, "E787", {"start": v(502.23, -142.28) * mm, "end": v(502.23, -160.54) * mm});
            skLineSegment(sketch, "E788", {"start": v(502.23, -160.54) * mm, "end": v(502.11, -161.9) * mm});
            skLineSegment(sketch, "E789", {"start": v(502.11, -161.9) * mm, "end": v(501.4, -162.04) * mm});
            skLineSegment(sketch, "E790", {"start": v(501.4, -162.04) * mm, "end": v(493.48, -162.04) * mm});
            skLineSegment(sketch, "E791", {"start": v(493.48, -162.04) * mm, "end": v(492.98, -161.96) * mm});
            skLineSegment(sketch, "E792", {"start": v(492.98, -161.96) * mm, "end": v(492.73, -160.52) * mm});
            skLineSegment(sketch, "E793", {"start": v(492.73, -160.52) * mm, "end": v(492.72, -148.43) * mm});
            skLineSegment(sketch, "E794", {"start": v(492.72, -148.43) * mm, "end": v(492.7, -147.04) * mm});
            skLineSegment(sketch, "E795", {"start": v(492.7, -147.04) * mm, "end": v(490.83, -146.52) * mm});
            skLineSegment(sketch, "E796", {"start": v(490.83, -146.52) * mm, "end": v(490.8, -146.16) * mm});
            skLineSegment(sketch, "E797", {"start": v(490.8, -146.16) * mm, "end": v(492.82, -140.9) * mm});
            skLineSegment(sketch, "E798", {"start": v(379.85, -161.96) * mm, "end": v(379.58, -160.14) * mm});
            skLineSegment(sketch, "E799", {"start": v(379.58, -160.14) * mm, "end": v(379.57, -148.45) * mm});
            skLineSegment(sketch, "E800", {"start": v(379.57, -148.45) * mm, "end": v(379.38, -146.83) * mm});
            skLineSegment(sketch, "E801", {"start": v(379.38, -146.83) * mm, "end": v(377.76, -146.61) * mm});
            skLineSegment(sketch, "E802", {"start": v(377.76, -146.61) * mm, "end": v(377.72, -146.08) * mm});
            skLineSegment(sketch, "E803", {"start": v(377.72, -146.08) * mm, "end": v(379.7, -141.09) * mm});
            skLineSegment(sketch, "E804", {"start": v(379.7, -141.09) * mm, "end": v(381.25, -140.75) * mm});
            skLineSegment(sketch, "E805", {"start": v(381.25, -140.75) * mm, "end": v(388.91, -140.98) * mm});
            skLineSegment(sketch, "E806", {"start": v(388.91, -140.98) * mm, "end": v(389.08, -142.38) * mm});
            skLineSegment(sketch, "E807", {"start": v(389.08, -142.38) * mm, "end": v(389.09, -153.13) * mm});
            skLineSegment(sketch, "E808", {"start": v(389.09, -153.13) * mm, "end": v(389.09, -160.38) * mm});
            skLineSegment(sketch, "E809", {"start": v(389.09, -160.38) * mm, "end": v(389.03, -161.89) * mm});
            skLineSegment(sketch, "E810", {"start": v(389.03, -161.89) * mm, "end": v(388.2, -162.05) * mm});
            skLineSegment(sketch, "E811", {"start": v(388.2, -162.05) * mm, "end": v(380.4, -162.05) * mm});
            skLineSegment(sketch, "E812", {"start": v(380.4, -162.05) * mm, "end": v(379.85, -161.96) * mm});
            skLineSegment(sketch, "E813", {"start": v(388.93, -132.75) * mm, "end": v(388.96, -138.96) * mm});
            skLineSegment(sketch, "E814", {"start": v(388.96, -138.96) * mm, "end": v(388.26, -139.17) * mm});
            skLineSegment(sketch, "E815", {"start": v(388.26, -139.17) * mm, "end": v(380.21, -139.15) * mm});
            skLineSegment(sketch, "E816", {"start": v(380.21, -139.15) * mm, "end": v(379.85, -139.05) * mm});
            skLineSegment(sketch, "E817", {"start": v(379.85, -139.05) * mm, "end": v(379.6, -138.26) * mm});
            skLineSegment(sketch, "E818", {"start": v(379.6, -138.26) * mm, "end": v(379.6, -133.57) * mm});
            skLineSegment(sketch, "E819", {"start": v(379.6, -133.57) * mm, "end": v(380.59, -132.6) * mm});
            skLineSegment(sketch, "E820", {"start": v(380.59, -132.6) * mm, "end": v(388.23, -132.6) * mm});
            skLineSegment(sketch, "E821", {"start": v(388.23, -132.6) * mm, "end": v(388.93, -132.75) * mm});
            skLineSegment(sketch, "E822", {"start": v(492.83, -138.87) * mm, "end": v(492.87, -132.8) * mm});
            skLineSegment(sketch, "E823", {"start": v(492.87, -132.8) * mm, "end": v(493.72, -132.6) * mm});
            skLineSegment(sketch, "E824", {"start": v(493.72, -132.6) * mm, "end": v(501.1, -132.59) * mm});
            skLineSegment(sketch, "E825", {"start": v(501.1, -132.59) * mm, "end": v(501.5, -132.61) * mm});
            skLineSegment(sketch, "E826", {"start": v(501.5, -132.61) * mm, "end": v(502.18, -133.3) * mm});
            skLineSegment(sketch, "E827", {"start": v(502.18, -133.3) * mm, "end": v(502.22, -133.84) * mm});
            skLineSegment(sketch, "E828", {"start": v(502.22, -133.84) * mm, "end": v(502.22, -138) * mm});
            skLineSegment(sketch, "E829", {"start": v(502.22, -138) * mm, "end": v(502.06, -138.98) * mm});
            skLineSegment(sketch, "E830", {"start": v(502.06, -138.98) * mm, "end": v(500.4, -139.18) * mm});
            skLineSegment(sketch, "E831", {"start": v(500.4, -139.18) * mm, "end": v(493.03, -139.07) * mm});
            skLineSegment(sketch, "E832", {"start": v(493.03, -139.07) * mm, "end": v(492.83, -138.87) * mm});
            skLineSegment(sketch, "E833.trimOffspring", {"start": v(-399.77, -3.7) * mm, "end": v(-405.36, -3.71) * mm});
            skLineSegment(sketch, "E834", {"start": v(363.92, -153.86) * mm, "end": v(363.91, -148.94) * mm});
            skLineSegment(sketch, "E835.trimOffspring", {"start": v(364.63, -148.96) * mm, "end": v(364.63, -153.86) * mm});
            skLineSegment(sketch, "E836.trimOffspring", {"start": v(363.92, -153.86) * mm, "end": v(360.4, -153.86) * mm});
            skLineSegment(sketch, "E837.trimOffspring", {"start": v(364.63, -148.96) * mm, "end": v(365.65, -148.98) * mm});
            skLineSegment(sketch, "E838", {"start": v(430.9, -148.29) * mm, "end": v(430.92, -152.93) * mm});
            skPoint(sketch, "E838.endSnap0", {"position": v(429.3, -154.23) * mm});
            skLineSegment(sketch, "E839", {"start": v(431.41, -152.93) * mm, "end": v(431.4, -148.02) * mm});
            skLineSegment(sketch, "E840.trimOffspring", {"start": v(430.92, -152.93) * mm, "end": v(429.34, -152.93) * mm});
            skLineSegment(sketch, "E841", {"start": v(457.95, -148.22) * mm, "end": v(457.95, -152.91) * mm});
            skLineSegment(sketch, "E842", {"start": v(457.46, -152.91) * mm, "end": v(457.46, -148.53) * mm});
            skLineSegment(sketch, "E843.trimOffspring", {"start": v(457.95, -148.22) * mm, "end": v(458.31, -147.99) * mm});
            skLineSegment(sketch, "E844.trimOffspring", {"start": v(457.46, -152.91) * mm, "end": v(455.77, -152.91) * mm});
            skLineSegment(sketch, "E845", {"start": v(544.1, -149.03) * mm, "end": v(544.1, -153.86) * mm});
            skLineSegment(sketch, "E846", {"start": v(544.87, -153.86) * mm, "end": v(544.87, -149.03) * mm});
            skLineSegment(sketch, "E847.trimOffspring", {"start": v(544.87, -149.03) * mm, "end": v(545.84, -149.03) * mm});
            skLineSegment(sketch, "E848.trimOffspring", {"start": v(544.1, -153.86) * mm, "end": v(541.17, -153.86) * mm});
            skLineSegment(sketch, "E849", {"start": v(-399.27, -60.2) * mm, "end": v(-399.27, -88.57) * mm});
            skLineSegment(sketch, "E850", {"start": v(-394.27, -60.21) * mm, "end": v(-394.18, -88.9) * mm});
            skLineSegment(sketch, "E851", {"start": v(-399.77, -3.7) * mm, "end": v(-394.77, -3.69) * mm});
            skSolve(sketch);
        }
        {
            var Q0;
            Q0 = qSketchRegion(id + "F0", true);
            extrude(context, id + "F2", {"entities" : qUnion([Q0]), "depth" : 25.4 * mm});
        }
        {
            var Q0;
            Q0 = qSketchRegion(id + "F1", true);
            extrude(context, id + "F3", {"entities" : qUnion([Q0]), "operationType" : NewBodyOperationType.REMOVE, "depth" : 25.4 * mm});
        }
    });
